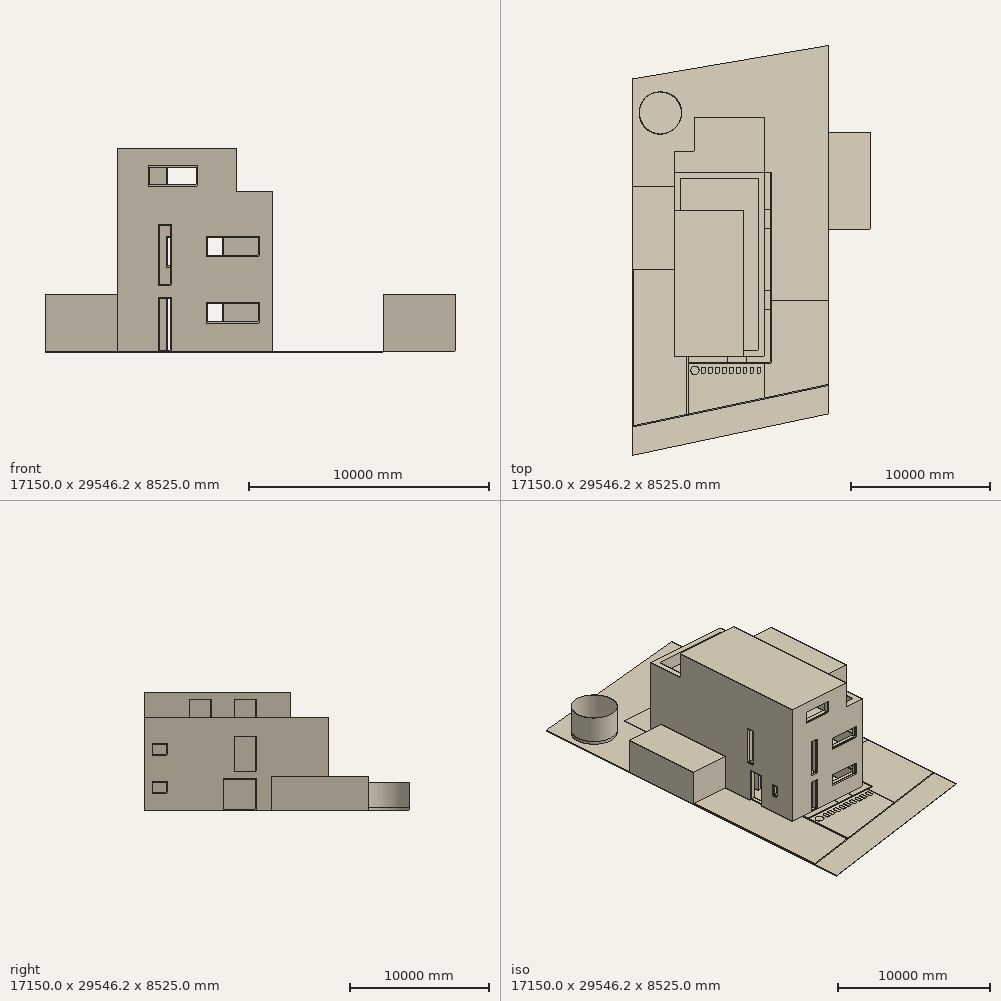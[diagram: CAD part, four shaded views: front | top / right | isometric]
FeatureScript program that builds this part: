
annotation { "Feature Type Name" : "Feature", "Feature Type Description" : "" }
export const myFeature = defineFeature(function(context is Context, id is Id, definition is map)
    precondition{}
    {
        {
            var Q0;
            Q0=qCreatedBy(makeId("Top.planeOp"),FACE);
            var sketch = newSketch(context, id + "F0", { "sketchPlane" : qUnion([Q0])});
            skLineSegment(sketch, "E0.bottom", {"start": v(0, 13250) * mm, "end": v(6500, 13250) * mm});
            skLineSegment(sketch, "E0.top", {"start": v(0, 0) * mm, "end": v(6500, 0) * mm});
            skLineSegment(sketch, "E0.left", {"start": v(0, 13250) * mm, "end": v(0, 0) * mm});
            skLineSegment(sketch, "E0.right", {"start": v(6500, 13250) * mm, "end": v(6500, 0) * mm});
            skSolve(sketch);
        }
        {
            var Q0;
            Q0=qCreatedBy(makeId("Top.planeOp"),FACE);
            var sketch = newSketch(context, id + "F1", { "sketchPlane" : qUnion([Q0])});
            skLineSegment(sketch, "E1", {"start": v(2050, 13250) * mm, "end": v(0, 13250) * mm});
            skLineSegment(sketch, "E2", {"start": v(0, 13250) * mm, "end": v(0, 4000) * mm});
            skLineSegment(sketch, "E3", {"start": v(0, 4000) * mm, "end": v(365, 4000) * mm});
            skLineSegment(sketch, "E4", {"start": v(365, 4000) * mm, "end": v(365, 12885) * mm});
            skLineSegment(sketch, "E5", {"start": v(365, 12885) * mm, "end": v(2050, 12885) * mm});
            skLineSegment(sketch, "E6", {"start": v(2050, 12885) * mm, "end": v(2050, 13250) * mm});
            skLineSegment(sketch, "E7", {"start": v(2050, 13067.5) * mm, "end": v(4450, 13067.5) * mm, "construction": true});
            skLineSegment(sketch, "E8", {"start": v(4450, 12885) * mm, "end": v(4450, 13250) * mm});
            skLineSegment(sketch, "E9", {"start": v(4450, 13250) * mm, "end": v(6500, 13250) * mm});
            skLineSegment(sketch, "E10", {"start": v(6500, 13250) * mm, "end": v(6500, 8065) * mm});
            skLineSegment(sketch, "E11", {"start": v(6500, 8065) * mm, "end": v(6135, 8065) * mm});
            skLineSegment(sketch, "E12", {"start": v(6135, 8065) * mm, "end": v(6135, 12885) * mm});
            skLineSegment(sketch, "E13", {"start": v(6135, 12885) * mm, "end": v(4450, 12885) * mm});
            skLineSegment(sketch, "E14", {"start": v(6317.5, 8065) * mm, "end": v(6317.5, 5665) * mm, "construction": true});
            skLineSegment(sketch, "E15.bottom", {"start": v(6135, 5665) * mm, "end": v(6500, 5665) * mm});
            skLineSegment(sketch, "E15.top", {"start": v(6135, 1655) * mm, "end": v(6500, 1655) * mm, "construction": true});
            skLineSegment(sketch, "E15.left", {"start": v(6135, 5665) * mm, "end": v(6135, 1655) * mm});
            skLineSegment(sketch, "E15.right", {"start": v(6500, 5665) * mm, "end": v(6500, 1655) * mm});
            skLineSegment(sketch, "E16", {"start": v(6135, 1655) * mm, "end": v(6135, 555) * mm});
            skLineSegment(sketch, "E17", {"start": v(6135, 555) * mm, "end": v(6500, 555) * mm, "construction": true});
            skLineSegment(sketch, "E18", {"start": v(6500, 555) * mm, "end": v(6500, 1655) * mm});
            skLineSegment(sketch, "E19", {"start": v(6135, 555) * mm, "end": v(6135, 365) * mm});
            skLineSegment(sketch, "E20", {"start": v(6135, 365) * mm, "end": v(5945, 365) * mm});
            skLineSegment(sketch, "E21", {"start": v(5945, 365) * mm, "end": v(5945, 0) * mm, "construction": true});
            skLineSegment(sketch, "E22", {"start": v(5945, 0) * mm, "end": v(6500, 0) * mm});
            skLineSegment(sketch, "E23", {"start": v(6500, 0) * mm, "end": v(6500, 555) * mm});
            skLineSegment(sketch, "E24", {"start": v(5945, 365) * mm, "end": v(3745, 365) * mm});
            skLineSegment(sketch, "E25", {"start": v(3745, 365) * mm, "end": v(3745, 0) * mm, "construction": true});
            skLineSegment(sketch, "E26", {"start": v(3745, 0) * mm, "end": v(5945, 0) * mm});
            skLineSegment(sketch, "E27", {"start": v(3745, 365) * mm, "end": v(2280, 365) * mm});
            skLineSegment(sketch, "E28", {"start": v(2280, 365) * mm, "end": v(2280, 0) * mm});
            skLineSegment(sketch, "E29", {"start": v(2280, 0) * mm, "end": v(3745, 0) * mm});
            skLineSegment(sketch, "E30", {"start": v(2280, 365) * mm, "end": v(1710, 365) * mm, "construction": true});
            skLineSegment(sketch, "E31", {"start": v(1710, 365) * mm, "end": v(1710, 0) * mm});
            skLineSegment(sketch, "E32", {"start": v(1710, 0) * mm, "end": v(2280, 0) * mm, "construction": true});
            skLineSegment(sketch, "E33", {"start": v(1710, 0) * mm, "end": v(0, 0) * mm});
            skLineSegment(sketch, "E34", {"start": v(0, 0) * mm, "end": v(0, 1400) * mm});
            skLineSegment(sketch, "E35", {"start": v(0, 1400) * mm, "end": v(365, 1400) * mm, "construction": true});
            skLineSegment(sketch, "E36", {"start": v(365, 1400) * mm, "end": v(365, 365) * mm});
            skLineSegment(sketch, "E37", {"start": v(365, 365) * mm, "end": v(1710, 365) * mm});
            skLineSegment(sketch, "E38", {"start": v(0, 1400) * mm, "end": v(0, 1900) * mm});
            skLineSegment(sketch, "E39", {"start": v(0, 1900) * mm, "end": v(365, 1900) * mm, "construction": true});
            skLineSegment(sketch, "E40", {"start": v(365, 1900) * mm, "end": v(365, 1400) * mm});
            skLineSegment(sketch, "E41", {"start": v(0, 1900) * mm, "end": v(0, 2900) * mm});
            skLineSegment(sketch, "E42", {"start": v(0, 2900) * mm, "end": v(365, 2900) * mm});
            skLineSegment(sketch, "E43", {"start": v(365, 2900) * mm, "end": v(365, 1900) * mm});
            skLineSegment(sketch, "E44", {"start": v(182.5, 2900) * mm, "end": v(182.5, 4000) * mm, "construction": true});
            skLineSegment(sketch, "E45.bottom", {"start": v(1305, 4500) * mm, "end": v(1455, 4500) * mm});
            skLineSegment(sketch, "E45.top", {"start": v(1305, 8000) * mm, "end": v(1455, 8000) * mm});
            skLineSegment(sketch, "E45.left", {"start": v(1305, 4500) * mm, "end": v(1305, 8000) * mm});
            skLineSegment(sketch, "E45.right", {"start": v(1455, 4500) * mm, "end": v(1455, 8000) * mm});
            skLineSegment(sketch, "E46", {"start": v(365, 2900) * mm, "end": v(1455, 2900) * mm});
            skLineSegment(sketch, "E47", {"start": v(1455, 2900) * mm, "end": v(1455, 365) * mm});
            skLineSegment(sketch, "E48", {"start": v(2955, 365) * mm, "end": v(2955, 2760) * mm});
            skLineSegment(sketch, "E49", {"start": v(2955, 2760) * mm, "end": v(2455, 2760) * mm});
            skLineSegment(sketch, "E50", {"start": v(2455, 2760) * mm, "end": v(2455, 2860) * mm});
            skLineSegment(sketch, "E51", {"start": v(2455, 2860) * mm, "end": v(3055, 2860) * mm});
            skLineSegment(sketch, "E52", {"start": v(3055, 2860) * mm, "end": v(3055, 365) * mm});
            skLineSegment(sketch, "E53.bottom", {"start": v(365, 2750) * mm, "end": v(1355, 2750) * mm});
            skLineSegment(sketch, "E53.right", {"start": v(1355, 2750) * mm, "end": v(1355, 365) * mm});
            skSolve(sketch);
        }
        {
            var Q0;
            Q0 = qSketchRegion(id + "F0", true);
            extrude(context, id + "F2", {"entities" : qUnion([Q0]), "oppositeDirection" : true, "depth" : 25 * mm, "offsetDistance" : 25 * mm});
        }
        {
            var Q0;
            Q0 = qSketchRegion(id + "F1", true);
            extrude(context, id + "F3", {"entities" : qUnion([Q0]), "depth" : 2270 * mm, "offsetDistance" : 25 * mm});
        }
        {
            var Q0;
            Q0=qCreatedBy(makeId("Top.planeOp"),FACE);
            cPlane(context, id + "F4", {"entities" : qUnion([Q0]), "cplaneType" : CPlaneType.OFFSET, "offset" : 1200 * mm, "width" : 150 * mm, "height" : 150 * mm});
        }
        {
            var Q0;
            Q0=qCreatedBy(id+"F4.planeOp",FACE);
            var sketch = newSketch(context, id + "F5", { "sketchPlane" : qUnion([Q0])});
            skLineSegment(sketch, "E54.bottom", {"start": v(6135, 1655) * mm, "end": v(6500, 1655) * mm});
            skLineSegment(sketch, "E54.top", {"start": v(6135, 555) * mm, "end": v(6500, 555) * mm});
            skLineSegment(sketch, "E54.left", {"start": v(6135, 1655) * mm, "end": v(6135, 555) * mm});
            skLineSegment(sketch, "E54.right", {"start": v(6500, 1655) * mm, "end": v(6500, 555) * mm});
            skLineSegment(sketch, "E55.bottom", {"start": v(5945, 365) * mm, "end": v(3745, 365) * mm});
            skLineSegment(sketch, "E55.top", {"start": v(5945, 0) * mm, "end": v(3745, 0) * mm});
            skLineSegment(sketch, "E55.left", {"start": v(5945, 365) * mm, "end": v(5945, 0) * mm});
            skLineSegment(sketch, "E55.right", {"start": v(3745, 365) * mm, "end": v(3745, 0) * mm});
            skLineSegment(sketch, "E56.bottom", {"start": v(365, 1400) * mm, "end": v(0, 1400) * mm});
            skLineSegment(sketch, "E56.top", {"start": v(365, 1900) * mm, "end": v(0, 1900) * mm});
            skLineSegment(sketch, "E56.left", {"start": v(0, 1900) * mm, "end": v(0, 1400) * mm});
            skLineSegment(sketch, "E56.right", {"start": v(365, 1900) * mm, "end": v(365, 1400) * mm});
            skSolve(sketch);
        }
        {
            var Q0;
            Q0 = qSketchRegion(id + "F5", true);
            extrude(context, id + "F6", {"entities" : qUnion([Q0]), "operationType" : NewBodyOperationType.REMOVE, "depth" : 850 * mm, "offsetDistance" : 25 * mm});
        }
        {
            var Q0;
            Q0=makeQuery(id+"F3.opExtrude","CAP_FACE",FACE,{"disambiguationData":[OSD([sQuery(id+"F1.wireOp",EDGE,"E31"),sQuery(id+"F1.wireOp",EDGE,"E33"),sQuery(id+"F1.wireOp",EDGE,"E34"),sQuery(id+"F1.wireOp",EDGE,"E36"),sQuery(id+"F1.wireOp",EDGE,"E37"),sQuery(id+"F1.wireOp",EDGE,"E38"),sQuery(id+"F1.wireOp",EDGE,"E40"),sQuery(id+"F1.wireOp",EDGE,"E41"),sQuery(id+"F1.wireOp",EDGE,"E42"),sQuery(id+"F1.wireOp",EDGE,"E43"),sQuery(id+"F1.wireOp",EDGE,"E46"),sQuery(id+"F1.wireOp",EDGE,"E47"),sQuery(id+"F1.wireOp",EDGE,"E53.bottom"),sQuery(id+"F1.wireOp",EDGE,"E53.right")])],"isStart":false});
            var sketch = newSketch(context, id + "F7", { "sketchPlane" : qUnion([Q0])});
            skLineSegment(sketch, "E57.bottom", {"start": v(0, 0) * mm, "end": v(6500, 0) * mm});
            skLineSegment(sketch, "E57.top", {"start": v(0, 13250) * mm, "end": v(6500, 13250) * mm});
            skLineSegment(sketch, "E57.left", {"start": v(0, 0) * mm, "end": v(0, 13250) * mm});
            skLineSegment(sketch, "E57.right", {"start": v(6500, 0) * mm, "end": v(6500, 13250) * mm});
            skLineSegment(sketch, "E58.bottom", {"start": v(365, 12885) * mm, "end": v(6135, 12885) * mm});
            skLineSegment(sketch, "E58.top", {"start": v(365, 365) * mm, "end": v(1355, 365) * mm});
            skLineSegment(sketch, "E58.left", {"start": v(365, 12885) * mm, "end": v(365, 2900) * mm});
            skLineSegment(sketch, "E58.right", {"start": v(6135, 12885) * mm, "end": v(6135, 365) * mm});
            skLineSegment(sketch, "E59", {"start": v(365, 2750) * mm, "end": v(1355, 2750) * mm});
            skLineSegment(sketch, "E60", {"start": v(1355, 2750) * mm, "end": v(1355, 365) * mm});
            skLineSegment(sketch, "E61", {"start": v(365, 2900) * mm, "end": v(1455, 2900) * mm});
            skLineSegment(sketch, "E62", {"start": v(1455, 2900) * mm, "end": v(1455, 365) * mm});
            skLineSegment(sketch, "E63", {"start": v(2955, 365) * mm, "end": v(2955, 2760) * mm});
            skLineSegment(sketch, "E64", {"start": v(2955, 2760) * mm, "end": v(2455, 2760) * mm});
            skLineSegment(sketch, "E65", {"start": v(2455, 2760) * mm, "end": v(2455, 2860) * mm});
            skLineSegment(sketch, "E66", {"start": v(2455, 2860) * mm, "end": v(3055, 2860) * mm});
            skLineSegment(sketch, "E67", {"start": v(3055, 2860) * mm, "end": v(3055, 365) * mm});
            skLineSegment(sketch, "E68.bottom", {"start": v(1305, 4500) * mm, "end": v(1455, 4500) * mm});
            skLineSegment(sketch, "E68.top", {"start": v(1305, 8000) * mm, "end": v(1455, 8000) * mm});
            skLineSegment(sketch, "E68.left", {"start": v(1305, 4500) * mm, "end": v(1305, 8000) * mm});
            skLineSegment(sketch, "E68.right", {"start": v(1455, 4500) * mm, "end": v(1455, 8000) * mm});
            skLineSegment(sketch, "E69.trimOffspring", {"start": v(3055, 365) * mm, "end": v(6135, 365) * mm});
            skLineSegment(sketch, "E70.trimOffspring", {"start": v(1455, 365) * mm, "end": v(2955, 365) * mm});
            skLineSegment(sketch, "E71.trimOffspring", {"start": v(365, 2750) * mm, "end": v(365, 365) * mm});
            skSolve(sketch);
        }
        {
            var Q0;
            Q0 = qSketchRegion(id + "F7", true);
            extrude(context, id + "F8", {"entities" : qUnion([Q0]), "operationType" : NewBodyOperationType.ADD, "depth" : 300 * mm, "offsetDistance" : 25 * mm});
        }
        {
            var Q0;
            Q0=makeQuery(id+"F3.opExtrude","CAP_FACE",FACE,{"disambiguationData":[OSD([sQuery(id+"F1.wireOp",EDGE,"E45.bottom"),sQuery(id+"F1.wireOp",EDGE,"E45.top"),sQuery(id+"F1.wireOp",EDGE,"E45.left"),sQuery(id+"F1.wireOp",EDGE,"E45.right")])],"isStart":false});
            var sketch = newSketch(context, id + "F9", { "sketchPlane" : qUnion([Q0])});
            skLineSegment(sketch, "E72.bottom", {"start": v(1305, 8000) * mm, "end": v(1455, 8000) * mm});
            skLineSegment(sketch, "E72.top", {"start": v(1305, 4500) * mm, "end": v(1455, 4500) * mm});
            skLineSegment(sketch, "E72.left", {"start": v(1305, 8000) * mm, "end": v(1305, 4500) * mm});
            skLineSegment(sketch, "E72.right", {"start": v(1455, 8000) * mm, "end": v(1455, 4500) * mm});
            skSolve(sketch);
        }
        {
            var Q0;
            Q0 = qSketchRegion(id + "F9", true);
            extrude(context, id + "F10", {"entities" : qUnion([Q0]), "operationType" : NewBodyOperationType.ADD, "depth" : 300 * mm, "offsetDistance" : 25 * mm});
        }
        {
            var Q0;
            Q0=makeQuery(id+"F8.opExtrude","CAP_FACE",FACE,{"disambiguationData":[OSD([sQuery(id+"F7.wireOp",EDGE,"E57.bottom"),sQuery(id+"F7.wireOp",EDGE,"E57.top"),sQuery(id+"F7.wireOp",EDGE,"E57.left"),sQuery(id+"F7.wireOp",EDGE,"E57.right"),sQuery(id+"F7.wireOp",EDGE,"E58.bottom"),sQuery(id+"F7.wireOp",EDGE,"E58.top"),sQuery(id+"F7.wireOp",EDGE,"E58.left"),sQuery(id+"F7.wireOp",EDGE,"E58.right"),sQuery(id+"F7.wireOp",EDGE,"E59"),sQuery(id+"F7.wireOp",EDGE,"E60"),sQuery(id+"F7.wireOp",EDGE,"E61"),sQuery(id+"F7.wireOp",EDGE,"E62"),sQuery(id+"F7.wireOp",EDGE,"E63"),sQuery(id+"F7.wireOp",EDGE,"E64"),sQuery(id+"F7.wireOp",EDGE,"E65"),sQuery(id+"F7.wireOp",EDGE,"E66"),sQuery(id+"F7.wireOp",EDGE,"E67"),sQuery(id+"F7.wireOp",EDGE,"E69.trimOffspring"),sQuery(id+"F7.wireOp",EDGE,"E70.trimOffspring"),sQuery(id+"F7.wireOp",EDGE,"E71.trimOffspring")])],"isStart":false});
            var sketch = newSketch(context, id + "F11", { "sketchPlane" : qUnion([Q0])});
            skLineSegment(sketch, "E73.bottom", {"start": v(0, 13250) * mm, "end": v(6500, 13250) * mm});
            skLineSegment(sketch, "E73.top", {"start": v(0, 0) * mm, "end": v(6500, 0) * mm});
            skLineSegment(sketch, "E73.left", {"start": v(0, 13250) * mm, "end": v(0, 0) * mm});
            skLineSegment(sketch, "E73.right", {"start": v(6500, 13250) * mm, "end": v(6500, 0) * mm});
            skSolve(sketch);
        }
        {
            var Q0;
            Q0 = qSketchRegion(id + "F11", true);
            extrude(context, id + "F12", {"entities" : qUnion([Q0]), "operationType" : NewBodyOperationType.ADD, "depth" : 200 * mm, "offsetDistance" : 25 * mm});
        }
        {
            var Q0;
            Q0=makeQuery(id+"F12.opExtrude","CAP_FACE",FACE,{"disambiguationData":[OSD([sQuery(id+"F11.wireOp",EDGE,"E73.bottom"),sQuery(id+"F11.wireOp",EDGE,"E73.top"),sQuery(id+"F11.wireOp",EDGE,"E73.left"),sQuery(id+"F11.wireOp",EDGE,"E73.right")])],"isStart":false});
            var sketch = newSketch(context, id + "F13", { "sketchPlane" : qUnion([Q0])});
            skLineSegment(sketch, "E74.bottom", {"start": v(0, 13250) * mm, "end": v(2050, 13250) * mm});
            skLineSegment(sketch, "E74.top", {"start": v(0, 0) * mm, "end": v(1710, 0) * mm});
            skLineSegment(sketch, "E74.left", {"start": v(0, 13250) * mm, "end": v(0, 4210) * mm});
            skLineSegment(sketch, "E74.right", {"start": v(6500, 13250) * mm, "end": v(6500, 8065) * mm});
            skLineSegment(sketch, "E75.bottom", {"start": v(365, 12885) * mm, "end": v(2050, 12885) * mm});
            skLineSegment(sketch, "E75.top", {"start": v(365, 365) * mm, "end": v(1710, 365) * mm});
            skLineSegment(sketch, "E75.left", {"start": v(365, 12885) * mm, "end": v(365, 4210) * mm});
            skLineSegment(sketch, "E75.right", {"start": v(6135, 12885) * mm, "end": v(6135, 8065) * mm});
            skLineSegment(sketch, "E76", {"start": v(2050, 13250) * mm, "end": v(2050, 12885) * mm, "construction": true});
            skLineSegment(sketch, "E77", {"start": v(2050, 13250) * mm, "end": v(4450, 13250) * mm});
            skLineSegment(sketch, "E78", {"start": v(4450, 12885) * mm, "end": v(6135, 12885) * mm});
            skLineSegment(sketch, "E79", {"start": v(2050, 12885) * mm, "end": v(4450, 12885) * mm});
            skLineSegment(sketch, "E80", {"start": v(4450, 13250) * mm, "end": v(4450, 12885) * mm, "construction": true});
            skLineSegment(sketch, "E81", {"start": v(4450, 13250) * mm, "end": v(6500, 13250) * mm});
            skLineSegment(sketch, "E82", {"start": v(6135, 8065) * mm, "end": v(6500, 8065) * mm});
            skLineSegment(sketch, "E83", {"start": v(6135, 6465) * mm, "end": v(6500, 6465) * mm});
            skLineSegment(sketch, "E84.trimOffspring", {"start": v(6135, 6465) * mm, "end": v(6135, 365) * mm});
            skLineSegment(sketch, "E85.trimOffspring", {"start": v(6500, 6465) * mm, "end": v(6500, 0) * mm});
            skLineSegment(sketch, "E86", {"start": v(6135, 1655) * mm, "end": v(6500, 1655) * mm, "construction": true});
            skLineSegment(sketch, "E87", {"start": v(6135, 555) * mm, "end": v(6500, 555) * mm, "construction": true});
            skLineSegment(sketch, "E88", {"start": v(5945, 365) * mm, "end": v(5945, 0) * mm, "construction": true});
            skLineSegment(sketch, "E89", {"start": v(3745, 365) * mm, "end": v(3745, 0) * mm, "construction": true});
            skLineSegment(sketch, "E90", {"start": v(1710, 365) * mm, "end": v(1710, 0) * mm});
            skLineSegment(sketch, "E91", {"start": v(2280, 365) * mm, "end": v(2280, 0) * mm});
            skLineSegment(sketch, "E92.trimOffspring", {"start": v(2280, 365) * mm, "end": v(6135, 365) * mm});
            skLineSegment(sketch, "E93.trimOffspring", {"start": v(2280, 0) * mm, "end": v(6500, 0) * mm});
            skLineSegment(sketch, "E94", {"start": v(0, 3640) * mm, "end": v(365, 3640) * mm});
            skLineSegment(sketch, "E95", {"start": v(0, 4210) * mm, "end": v(365, 4210) * mm});
            skLineSegment(sketch, "E96.trimOffspring", {"start": v(0, 3640) * mm, "end": v(0, 0) * mm});
            skLineSegment(sketch, "E97.trimOffspring", {"start": v(365, 3640) * mm, "end": v(365, 365) * mm});
            skSolve(sketch);
        }
        {
            var Q0;
            Q0 = qSketchRegion(id + "F13", true);
            extrude(context, id + "F14", {"entities" : qUnion([Q0]), "operationType" : NewBodyOperationType.ADD, "depth" : 2570 * mm, "offsetDistance" : 25 * mm});
        }
        {
            var Q0;
            Q0=makeQuery(id+"F12.opExtrude","CAP_FACE",FACE,{"disambiguationData":[OSD([sQuery(id+"F11.wireOp",EDGE,"E73.bottom"),sQuery(id+"F11.wireOp",EDGE,"E73.top"),sQuery(id+"F11.wireOp",EDGE,"E73.left"),sQuery(id+"F11.wireOp",EDGE,"E73.right")])],"isStart":false});
            cPlane(context, id + "F15", {"entities" : qUnion([Q0]), "cplaneType" : CPlaneType.OFFSET, "offset" : 1200 * mm, "width" : 150 * mm, "height" : 150 * mm});
        }
        {
            var Q0;
            Q0=qCreatedBy(id+"F15.planeOp",FACE);
            var sketch = newSketch(context, id + "F16", { "sketchPlane" : qUnion([Q0])});
            skLineSegment(sketch, "E98.bottom", {"start": v(3745, 365) * mm, "end": v(5945, 365) * mm});
            skLineSegment(sketch, "E98.top", {"start": v(3745, 0) * mm, "end": v(5945, 0) * mm});
            skLineSegment(sketch, "E98.left", {"start": v(3745, 365) * mm, "end": v(3745, 0) * mm});
            skLineSegment(sketch, "E98.right", {"start": v(5945, 365) * mm, "end": v(5945, 0) * mm});
            skLineSegment(sketch, "E99.bottom", {"start": v(6135, 1655) * mm, "end": v(6500, 1655) * mm});
            skLineSegment(sketch, "E99.top", {"start": v(6135, 555) * mm, "end": v(6500, 555) * mm});
            skLineSegment(sketch, "E99.left", {"start": v(6135, 1655) * mm, "end": v(6135, 555) * mm});
            skLineSegment(sketch, "E99.right", {"start": v(6500, 1655) * mm, "end": v(6500, 555) * mm});
            skSolve(sketch);
        }
        {
            var Q0;
            Q0 = qSketchRegion(id + "F16", true);
            extrude(context, id + "F17", {"entities" : qUnion([Q0]), "operationType" : NewBodyOperationType.REMOVE, "depth" : 850 * mm, "offsetDistance" : 25 * mm});
        }
        {
            var Q0;
            Q0=makeQuery(id+"F14.opExtrude","CAP_FACE",FACE,{"disambiguationData":[OSD([sQuery(id+"F13.wireOp",EDGE,"E74.bottom"),sQuery(id+"F13.wireOp",EDGE,"E74.left"),sQuery(id+"F13.wireOp",EDGE,"E74.right"),sQuery(id+"F13.wireOp",EDGE,"E75.bottom"),sQuery(id+"F13.wireOp",EDGE,"E75.left"),sQuery(id+"F13.wireOp",EDGE,"E75.right"),sQuery(id+"F13.wireOp",EDGE,"E77"),sQuery(id+"F13.wireOp",EDGE,"E78"),sQuery(id+"F13.wireOp",EDGE,"E79"),sQuery(id+"F13.wireOp",EDGE,"E81"),sQuery(id+"F13.wireOp",EDGE,"E82"),sQuery(id+"F13.wireOp",EDGE,"E95")])],"isStart":false});
            var sketch = newSketch(context, id + "F18", { "sketchPlane" : qUnion([Q0])});
            skLineSegment(sketch, "E100.bottom", {"start": v(0, 13250) * mm, "end": v(6500, 13250) * mm});
            skLineSegment(sketch, "E100.top", {"start": v(0, 0) * mm, "end": v(6500, 0) * mm});
            skLineSegment(sketch, "E100.left", {"start": v(0, 13250) * mm, "end": v(0, 0) * mm});
            skLineSegment(sketch, "E100.right", {"start": v(6500, 13250) * mm, "end": v(6500, 0) * mm});
            skLineSegment(sketch, "E101.bottom", {"start": v(365, 12885) * mm, "end": v(6135, 12885) * mm});
            skLineSegment(sketch, "E101.top", {"start": v(365, 365) * mm, "end": v(6135, 365) * mm});
            skLineSegment(sketch, "E101.left", {"start": v(365, 12885) * mm, "end": v(365, 365) * mm});
            skLineSegment(sketch, "E101.right", {"start": v(6135, 12885) * mm, "end": v(6135, 365) * mm});
            skSolve(sketch);
        }
        {
            var Q0;
            Q0 = qSketchRegion(id + "F18", true);
            extrude(context, id + "F19", {"entities" : qUnion([Q0]), "operationType" : NewBodyOperationType.ADD, "depth" : 300 * mm, "offsetDistance" : 25 * mm});
        }
        {
            var Q0;
            Q0=makeQuery(id+"F13.imprint","IMPRINT",FACE,{"disambiguationData":[TD([[makeQuery(id+"F13.imprint","IMPRINT",EDGE,{"derivedFrom":sQuery(id+"F13.wireOp",EDGE,"E75.bottom")}),-1.0]])]});
            cPlane(context, id + "F20", {"entities" : qUnion([Q0]), "cplaneType" : CPlaneType.OFFSET, "offset" : 770 * mm, "width" : 150 * mm, "height" : 150 * mm});
        }
        {
            var Q0;
            Q0=qCreatedBy(id+"F20.planeOp",FACE);
            var sketch = newSketch(context, id + "F21", { "sketchPlane" : qUnion([Q0])});
            skLineSegment(sketch, "E102.bottom", {"start": v(2050, 13250) * mm, "end": v(4450, 13250) * mm});
            skLineSegment(sketch, "E102.top", {"start": v(2050, 12885) * mm, "end": v(4450, 12885) * mm});
            skLineSegment(sketch, "E102.left", {"start": v(2050, 13250) * mm, "end": v(2050, 12885) * mm});
            skLineSegment(sketch, "E102.right", {"start": v(4450, 13250) * mm, "end": v(4450, 12885) * mm});
            skSolve(sketch);
        }
        {
            var Q0;
            Q0 = qSketchRegion(id + "F21", true);
            extrude(context, id + "F22", {"entities" : qUnion([Q0]), "operationType" : NewBodyOperationType.REMOVE, "depth" : 1280 * mm, "offsetDistance" : 25 * mm});
        }
        {
            var Q0;
            Q0=makeQuery(id+"F19.opExtrude","CAP_FACE",FACE,{"disambiguationData":[OSD([sQuery(id+"F18.wireOp",EDGE,"E100.bottom"),sQuery(id+"F18.wireOp",EDGE,"E100.top"),sQuery(id+"F18.wireOp",EDGE,"E100.left"),sQuery(id+"F18.wireOp",EDGE,"E100.right"),sQuery(id+"F18.wireOp",EDGE,"E101.bottom"),sQuery(id+"F18.wireOp",EDGE,"E101.top"),sQuery(id+"F18.wireOp",EDGE,"E101.left"),sQuery(id+"F18.wireOp",EDGE,"E101.right")])],"isStart":false});
            var sketch = newSketch(context, id + "F23", { "sketchPlane" : qUnion([Q0])});
            skLineSegment(sketch, "E103.bottom", {"start": v(0, 13250) * mm, "end": v(6500, 13250) * mm});
            skLineSegment(sketch, "E103.top", {"start": v(0, 0) * mm, "end": v(6500, 0) * mm});
            skLineSegment(sketch, "E103.left", {"start": v(0, 13250) * mm, "end": v(0, 0) * mm});
            skLineSegment(sketch, "E103.right", {"start": v(6500, 13250) * mm, "end": v(6500, 0) * mm});
            skSolve(sketch);
        }
        {
            var Q0;
            Q0 = qSketchRegion(id + "F23", true);
            extrude(context, id + "F24", {"entities" : qUnion([Q0]), "operationType" : NewBodyOperationType.ADD, "depth" : 200 * mm, "offsetDistance" : 25 * mm});
        }
        {
            var Q0;
            Q0=makeQuery(id+"F24.opExtrude","CAP_FACE",FACE,{"disambiguationData":[OSD([sQuery(id+"F23.wireOp",EDGE,"E103.bottom"),sQuery(id+"F23.wireOp",EDGE,"E103.top"),sQuery(id+"F23.wireOp",EDGE,"E103.left"),sQuery(id+"F23.wireOp",EDGE,"E103.right")])],"isStart":false});
            var sketch = newSketch(context, id + "F25", { "sketchPlane" : qUnion([Q0])});
            skLineSegment(sketch, "E104.bottom", {"start": v(0, 0) * mm, "end": v(1310, 0) * mm});
            skLineSegment(sketch, "E104.top", {"start": v(0, 10500) * mm, "end": v(2045, 10500) * mm});
            skLineSegment(sketch, "E104.left", {"start": v(0, 0) * mm, "end": v(0, 10500) * mm});
            skLineSegment(sketch, "E104.right", {"start": v(5000, 0) * mm, "end": v(5000, 3235) * mm});
            skLineSegment(sketch, "E105.bottom", {"start": v(365, 10135) * mm, "end": v(2045, 10135) * mm});
            skLineSegment(sketch, "E105.top", {"start": v(365, 365) * mm, "end": v(1310, 365) * mm});
            skLineSegment(sketch, "E105.left", {"start": v(365, 10135) * mm, "end": v(365, 365) * mm});
            skLineSegment(sketch, "E105.right", {"start": v(4635, 10135) * mm, "end": v(4635, 8065) * mm});
            skLineSegment(sketch, "E106", {"start": v(2045, 10135) * mm, "end": v(2045, 10500) * mm});
            skLineSegment(sketch, "E107", {"start": v(4445, 10500) * mm, "end": v(4445, 10135) * mm});
            skLineSegment(sketch, "E108.trimOffspring", {"start": v(4445, 10500) * mm, "end": v(5000, 10500) * mm});
            skLineSegment(sketch, "E109.trimOffspring", {"start": v(4445, 10135) * mm, "end": v(4635, 10135) * mm});
            skLineSegment(sketch, "E110", {"start": v(4635, 8065) * mm, "end": v(5000, 8065) * mm});
            skLineSegment(sketch, "E111", {"start": v(4635, 6465) * mm, "end": v(5000, 6465) * mm});
            skLineSegment(sketch, "E112.trimOffspring", {"start": v(4635, 6465) * mm, "end": v(4635, 4835) * mm});
            skLineSegment(sketch, "E113.trimOffspring", {"start": v(5000, 8065) * mm, "end": v(5000, 10500) * mm});
            skLineSegment(sketch, "E114", {"start": v(4635, 4835) * mm, "end": v(5000, 4835) * mm});
            skLineSegment(sketch, "E115", {"start": v(4635, 3235) * mm, "end": v(5000, 3235) * mm});
            skLineSegment(sketch, "E116.trimOffspring", {"start": v(4635, 3235) * mm, "end": v(4635, 365) * mm});
            skLineSegment(sketch, "E117.trimOffspring", {"start": v(5000, 4835) * mm, "end": v(5000, 6465) * mm});
            skLineSegment(sketch, "E118", {"start": v(3360, 365) * mm, "end": v(3360, 0) * mm, "construction": true});
            skLineSegment(sketch, "E119", {"start": v(1310, 365) * mm, "end": v(1310, 0) * mm, "construction": true});
            skLineSegment(sketch, "E120.trimOffspring", {"start": v(3360, 365) * mm, "end": v(4635, 365) * mm});
            skLineSegment(sketch, "E121.trimOffspring", {"start": v(3360, 0) * mm, "end": v(5000, 0) * mm});
            skLineSegment(sketch, "E122", {"start": v(365, 365) * mm, "end": v(0, 365) * mm, "construction": true});
            skLineSegment(sketch, "E123", {"start": v(1310, 365) * mm, "end": v(3360, 365) * mm});
            skLineSegment(sketch, "E124", {"start": v(1310, 0) * mm, "end": v(3360, 0) * mm});
            skSolve(sketch);
        }
        {
            var Q0;
            Q0 = qSketchRegion(id + "F25", true);
            extrude(context, id + "F26", {"entities" : qUnion([Q0]), "operationType" : NewBodyOperationType.ADD, "depth" : 2160 * mm, "offsetDistance" : 25 * mm});
        }
        {
            var Q0;
            Q0=makeQuery(id+"F24.opExtrude","CAP_FACE",FACE,{"disambiguationData":[OSD([sQuery(id+"F23.wireOp",EDGE,"E103.bottom"),sQuery(id+"F23.wireOp",EDGE,"E103.top"),sQuery(id+"F23.wireOp",EDGE,"E103.left"),sQuery(id+"F23.wireOp",EDGE,"E103.right")])],"isStart":false});
            cPlane(context, id + "F27", {"entities" : qUnion([Q0]), "cplaneType" : CPlaneType.OFFSET, "offset" : 1090 * mm, "width" : 150 * mm, "height" : 150 * mm});
        }
        {
            var Q0;
            Q0=qCreatedBy(id+"F27.planeOp",FACE);
            var sketch = newSketch(context, id + "F28", { "sketchPlane" : qUnion([Q0])});
            skLineSegment(sketch, "E125.bottom", {"start": v(1310, 365) * mm, "end": v(3360, 365) * mm});
            skLineSegment(sketch, "E125.top", {"start": v(1310, 0) * mm, "end": v(3360, 0) * mm});
            skLineSegment(sketch, "E125.left", {"start": v(1310, 365) * mm, "end": v(1310, 0) * mm});
            skLineSegment(sketch, "E125.right", {"start": v(3360, 365) * mm, "end": v(3360, 0) * mm});
            skSolve(sketch);
        }
        {
            var Q0;
            Q0 = qSketchRegion(id + "F28", true);
            extrude(context, id + "F29", {"entities" : qUnion([Q0]), "operationType" : NewBodyOperationType.REMOVE, "depth" : 850 * mm, "offsetDistance" : 25 * mm});
        }
        {
            var Q0;
            Q0=makeQuery(id+"F26.opExtrude","CAP_FACE",FACE,{"disambiguationData":[OSD([sQuery(id+"F25.wireOp",EDGE,"E104.bottom"),sQuery(id+"F25.wireOp",EDGE,"E104.top"),sQuery(id+"F25.wireOp",EDGE,"E104.left"),sQuery(id+"F25.wireOp",EDGE,"E104.right"),sQuery(id+"F25.wireOp",EDGE,"E105.bottom"),sQuery(id+"F25.wireOp",EDGE,"E105.top"),sQuery(id+"F25.wireOp",EDGE,"E105.left"),sQuery(id+"F25.wireOp",EDGE,"E106"),sQuery(id+"F25.wireOp",EDGE,"E115"),sQuery(id+"F25.wireOp",EDGE,"E116.trimOffspring"),sQuery(id+"F25.wireOp",EDGE,"E120.trimOffspring"),sQuery(id+"F25.wireOp",EDGE,"E121.trimOffspring"),sQuery(id+"F25.wireOp",EDGE,"E123"),sQuery(id+"F25.wireOp",EDGE,"E124")])],"isStart":false});
            var sketch = newSketch(context, id + "F30", { "sketchPlane" : qUnion([Q0])});
            skLineSegment(sketch, "E126.bottom", {"start": v(0, 10500) * mm, "end": v(5000, 10500) * mm});
            skLineSegment(sketch, "E126.top", {"start": v(0, 0) * mm, "end": v(5000, 0) * mm});
            skLineSegment(sketch, "E126.left", {"start": v(0, 10500) * mm, "end": v(0, 0) * mm});
            skLineSegment(sketch, "E126.right", {"start": v(5000, 10500) * mm, "end": v(5000, 0) * mm});
            skLineSegment(sketch, "E127.bottom", {"start": v(4635, 365) * mm, "end": v(365, 365) * mm});
            skLineSegment(sketch, "E127.top", {"start": v(4635, 10135) * mm, "end": v(365, 10135) * mm});
            skLineSegment(sketch, "E127.left", {"start": v(4635, 365) * mm, "end": v(4635, 10135) * mm});
            skLineSegment(sketch, "E127.right", {"start": v(365, 365) * mm, "end": v(365, 10135) * mm});
            skSolve(sketch);
        }
        {
            var Q0;
            Q0 = qSketchRegion(id + "F30", true);
            extrude(context, id + "F31", {"entities" : qUnion([Q0]), "operationType" : NewBodyOperationType.ADD, "depth" : 300 * mm, "offsetDistance" : 25 * mm});
        }
        {
            var Q0;
            Q0=makeQuery(id+"F31.opExtrude","CAP_FACE",FACE,{"disambiguationData":[OSD([sQuery(id+"F30.wireOp",EDGE,"E126.bottom"),sQuery(id+"F30.wireOp",EDGE,"E126.top"),sQuery(id+"F30.wireOp",EDGE,"E126.left"),sQuery(id+"F30.wireOp",EDGE,"E126.right"),sQuery(id+"F30.wireOp",EDGE,"E127.bottom"),sQuery(id+"F30.wireOp",EDGE,"E127.top"),sQuery(id+"F30.wireOp",EDGE,"E127.left"),sQuery(id+"F30.wireOp",EDGE,"E127.right")])],"isStart":false});
            var sketch = newSketch(context, id + "F32", { "sketchPlane" : qUnion([Q0])});
            skLineSegment(sketch, "E128.bottom", {"start": v(0, 10500) * mm, "end": v(5000, 10500) * mm});
            skLineSegment(sketch, "E128.top", {"start": v(0, 0) * mm, "end": v(5000, 0) * mm});
            skLineSegment(sketch, "E128.left", {"start": v(0, 10500) * mm, "end": v(0, 0) * mm});
            skLineSegment(sketch, "E128.right", {"start": v(5000, 10500) * mm, "end": v(5000, 0) * mm});
            skSolve(sketch);
        }
        {
            var Q0;
            Q0 = qSketchRegion(id + "F32", true);
            extrude(context, id + "F33", {"entities" : qUnion([Q0]), "operationType" : NewBodyOperationType.ADD, "depth" : 200 * mm, "offsetDistance" : 25 * mm});
        }
        {
            var Q0;
            Q0=makeQuery(id+"F24.opExtrude","CAP_FACE",FACE,{"disambiguationData":[OSD([sQuery(id+"F23.wireOp",EDGE,"E103.bottom"),sQuery(id+"F23.wireOp",EDGE,"E103.top"),sQuery(id+"F23.wireOp",EDGE,"E103.left"),sQuery(id+"F23.wireOp",EDGE,"E103.right")])],"isStart":false});
            var sketch = newSketch(context, id + "F34", { "sketchPlane" : qUnion([Q0])});
            skLineSegment(sketch, "E129", {"start": v(440, 10500) * mm, "end": v(0, 10500) * mm});
            skLineSegment(sketch, "E130", {"start": v(0, 10500) * mm, "end": v(0, 13250) * mm});
            skLineSegment(sketch, "E131", {"start": v(0, 13250) * mm, "end": v(6500, 13250) * mm});
            skLineSegment(sketch, "E132", {"start": v(6500, 13250) * mm, "end": v(6500, 0) * mm});
            skLineSegment(sketch, "E133", {"start": v(6500, 0) * mm, "end": v(5000, 0) * mm});
            skLineSegment(sketch, "E134", {"start": v(5000, 0) * mm, "end": v(5000, 440) * mm});
            skLineSegment(sketch, "E135", {"start": v(5000, 440) * mm, "end": v(6060, 440) * mm});
            skLineSegment(sketch, "E136", {"start": v(6060, 440) * mm, "end": v(6060, 12810) * mm});
            skLineSegment(sketch, "E137", {"start": v(6060, 12810) * mm, "end": v(440, 12810) * mm});
            skLineSegment(sketch, "E138", {"start": v(440, 12810) * mm, "end": v(440, 10500) * mm});
            skLineSegment(sketch, "E139", {"start": v(6060, 12810) * mm, "end": v(6060, 13250) * mm, "construction": true});
            skLineSegment(sketch, "E140", {"start": v(6060, 12810) * mm, "end": v(6500, 12810) * mm, "construction": true});
            skSolve(sketch);
        }
        {
            var Q0;
            Q0 = qSketchRegion(id + "F34", true);
            extrude(context, id + "F35", {"entities" : qUnion([Q0]), "operationType" : NewBodyOperationType.ADD, "depth" : 850 * mm, "offsetDistance" : 25 * mm});
        }
        {
            var Q0;
            Q0=qCreatedBy(makeId("Top.planeOp"),FACE);
            var sketch = newSketch(context, id + "F36", { "sketchPlane" : qUnion([Q0])});
            skLineSegment(sketch, "E141", {"start": v(-3000, -5000) * mm, "end": v(11150, -2000) * mm});
            skLineSegment(sketch, "E142", {"start": v(11150, -2000) * mm, "end": v(11150, 22420) * mm});
            skLineSegment(sketch, "E143", {"start": v(11150, 22420) * mm, "end": v(-3000, 20000) * mm});
            skLineSegment(sketch, "E144", {"start": v(-3000, 20000) * mm, "end": v(-3000, -5000) * mm});
            skSolve(sketch);
        }
        {
            var Q0;
            Q0=qCreatedBy(makeId("Top.planeOp"),FACE);
            var sketch = newSketch(context, id + "F37", { "sketchPlane" : qUnion([Q0])});
            skLineSegment(sketch, "E145.bottom", {"start": v(-2850, 6250) * mm, "end": v(-3000, 6250) * mm});
            skLineSegment(sketch, "E145.top", {"start": v(-2600, 12250) * mm, "end": v(-3000, 12250) * mm});
            skLineSegment(sketch, "E145.left", {"start": v(-3000, 6250) * mm, "end": v(-3000, 12250) * mm});
            skLineSegment(sketch, "E145.right", {"start": v(0, 6250) * mm, "end": v(0, 12250) * mm});
            skLineSegment(sketch, "E146.bottom", {"start": v(-2850, 12100) * mm, "end": v(-2600, 12100) * mm});
            skLineSegment(sketch, "E146.left", {"start": v(-2850, 12100) * mm, "end": v(-2850, 6250) * mm});
            skLineSegment(sketch, "E146.right", {"start": v(-150, 12100) * mm, "end": v(-150, 6250) * mm});
            skLineSegment(sketch, "E147", {"start": v(-2600, 12250) * mm, "end": v(-2600, 12100) * mm});
            skLineSegment(sketch, "E148", {"start": v(-1750, 12250) * mm, "end": v(-1750, 12100) * mm});
            skLineSegment(sketch, "E149.trimOffspring", {"start": v(0, 12250) * mm, "end": v(-1750, 12250) * mm});
            skLineSegment(sketch, "E150.trimOffspring", {"start": v(-1750, 12100) * mm, "end": v(-150, 12100) * mm});
            skLineSegment(sketch, "E151", {"start": v(-2850, 12100) * mm, "end": v(-3000, 12100) * mm, "construction": true});
            skLineSegment(sketch, "E152", {"start": v(-150, 12100) * mm, "end": v(0, 12100) * mm, "construction": true});
            skLineSegment(sketch, "E153", {"start": v(-2600, 12175) * mm, "end": v(-1750, 12175) * mm, "construction": true});
            skLineSegment(sketch, "E154.trimOffspring", {"start": v(0, 6250) * mm, "end": v(-150, 6250) * mm});
            skSolve(sketch);
        }
        {
            var Q0;
            Q0 = qSketchRegion(id + "F37", true);
            extrude(context, id + "F38", {"entities" : qUnion([Q0]), "operationType" : NewBodyOperationType.ADD, "depth" : 2200 * mm, "offsetDistance" : 25 * mm});
        }
        {
            var Q0;
            Q0=qCreatedBy(makeId("Top.planeOp"),FACE);
            var sketch = newSketch(context, id + "F39", { "sketchPlane" : qUnion([Q0])});
            skLineSegment(sketch, "E155.bottom", {"start": v(-3000, 12250) * mm, "end": v(0, 12250) * mm});
            skLineSegment(sketch, "E155.top", {"start": v(-3000, 6250) * mm, "end": v(0, 6250) * mm});
            skLineSegment(sketch, "E155.left", {"start": v(-3000, 12250) * mm, "end": v(-3000, 6250) * mm});
            skLineSegment(sketch, "E155.right", {"start": v(0, 12250) * mm, "end": v(0, 6250) * mm});
            skSolve(sketch);
        }
        {
            var Q0;
            Q0 = qSketchRegion(id + "F39", true);
            extrude(context, id + "F40", {"entities" : qUnion([Q0]), "operationType" : NewBodyOperationType.ADD, "oppositeDirection" : true, "depth" : 25 * mm, "offsetDistance" : 25 * mm});
        }
        {
            var Q0;
            Q0=makeQuery(id+"F38.opExtrude","CAP_FACE",FACE,{"disambiguationData":[OSD([sQuery(id+"F37.wireOp",EDGE,"E145.right"),sQuery(id+"F37.wireOp",EDGE,"E146.right"),sQuery(id+"F37.wireOp",EDGE,"E148"),sQuery(id+"F37.wireOp",EDGE,"E149.trimOffspring"),sQuery(id+"F37.wireOp",EDGE,"E150.trimOffspring"),sQuery(id+"F37.wireOp",EDGE,"E154.trimOffspring")])],"isStart":false});
            var sketch = newSketch(context, id + "F41", { "sketchPlane" : qUnion([Q0])});
            skLineSegment(sketch, "E156.bottom", {"start": v(-3000, 12250) * mm, "end": v(0, 12250) * mm});
            skLineSegment(sketch, "E156.top", {"start": v(-3000, 6250) * mm, "end": v(0, 6250) * mm});
            skLineSegment(sketch, "E156.left", {"start": v(-3000, 12250) * mm, "end": v(-3000, 6250) * mm});
            skLineSegment(sketch, "E156.right", {"start": v(0, 12250) * mm, "end": v(0, 6250) * mm});
            skSolve(sketch);
        }
        {
            var Q0;
            Q0 = qSketchRegion(id + "F41", true);
            extrude(context, id + "F42", {"entities" : qUnion([Q0]), "operationType" : NewBodyOperationType.ADD, "depth" : 200 * mm, "offsetDistance" : 25 * mm});
        }
        {
            var Q0;
            Q0=qCreatedBy(makeId("Top.planeOp"),FACE);
            var sketch = newSketch(context, id + "F43", { "sketchPlane" : qUnion([Q0])});
            skLineSegment(sketch, "E157", {"start": v(-3000, 6250) * mm, "end": v(-2920, 6250) * mm});
            skLineSegment(sketch, "E158", {"start": v(920, 0) * mm, "end": v(1000, 0) * mm});
            skLineSegment(sketch, "E159", {"start": v(1000, 0) * mm, "end": v(1000, -4151.94) * mm});
            skLineSegment(sketch, "E160", {"start": v(1000, -4151.94) * mm, "end": v(920, -4168.9) * mm});
            skLineSegment(sketch, "E161", {"start": v(-2920, -4983.04) * mm, "end": v(-2920, 6250) * mm});
            skLineSegment(sketch, "E162", {"start": v(920, 0) * mm, "end": v(920, -4168.9) * mm});
            skLineSegment(sketch, "E163", {"start": v(-3000, -5000) * mm, "end": v(-3000, 6250) * mm});
            skLineSegment(sketch, "E164.trimOffspring", {"start": v(-2920, -4983.04) * mm, "end": v(-3000, -5000) * mm});
            skSolve(sketch);
        }
        {
            var Q0;
            Q0=qSketchRegion(id+"F43",true);
            extrude(context, id + "F44", {"entities" : qUnion([Q0]), "oppositeDirection" : true, "depth" : 25 * mm, "offsetDistance" : 25 * mm});
        }
        {
            var Q0;
            Q0=qCreatedBy(makeId("Top.planeOp"),FACE);
            var sketch = newSketch(context, id + "F45", { "sketchPlane" : qUnion([Q0])});
            skLineSegment(sketch, "E165", {"start": v(-2920, -4983.04) * mm, "end": v(920, -4168.9) * mm});
            skLineSegment(sketch, "E166", {"start": v(920, -4168.9) * mm, "end": v(920, 0) * mm});
            skLineSegment(sketch, "E167", {"start": v(920, 0) * mm, "end": v(0, 0) * mm});
            skLineSegment(sketch, "E168", {"start": v(0, 0) * mm, "end": v(0, 6250) * mm});
            skLineSegment(sketch, "E169", {"start": v(0, 6250) * mm, "end": v(-2920, 6250) * mm});
            skLineSegment(sketch, "E170", {"start": v(-2920, 6250) * mm, "end": v(-2920, -4983.04) * mm});
            skSolve(sketch);
        }
        {
            var Q0;
            Q0 = qSketchRegion(id + "F45", true);
            extrude(context, id + "F46", {"entities" : qUnion([Q0]), "oppositeDirection" : true, "depth" : 25 * mm, "offsetDistance" : 25 * mm});
        }
        {
            var Q0;
            Q0=qCreatedBy(makeId("Top.planeOp"),FACE);
            var sketch = newSketch(context, id + "F47", { "sketchPlane" : qUnion([Q0])});
            skLineSegment(sketch, "E171", {"start": v(1000, 0) * mm, "end": v(1000, -420) * mm});
            skLineSegment(sketch, "E172", {"start": v(1000, -420) * mm, "end": v(3880, -420) * mm});
            skLineSegment(sketch, "E173", {"start": v(6920, -420) * mm, "end": v(6920, 3400) * mm});
            skLineSegment(sketch, "E174", {"start": v(6920, 13250) * mm, "end": v(6500, 13250) * mm});
            skLineSegment(sketch, "E175", {"start": v(6500, 13250) * mm, "end": v(6500, 10580) * mm});
            skLineSegment(sketch, "E176", {"start": v(6500, 0) * mm, "end": v(5230, 0) * mm});
            skLineSegment(sketch, "E177", {"start": v(5230, 0) * mm, "end": v(5230, -420) * mm});
            skLineSegment(sketch, "E178", {"start": v(3880, 0) * mm, "end": v(3880, -420) * mm});
            skLineSegment(sketch, "E179", {"start": v(6500, 10580) * mm, "end": v(6920, 10580) * mm});
            skLineSegment(sketch, "E180", {"start": v(6500, 9230) * mm, "end": v(6920, 9230) * mm});
            skLineSegment(sketch, "E181", {"start": v(6500, 3400) * mm, "end": v(6920, 3400) * mm});
            skLineSegment(sketch, "E182", {"start": v(6500, 4750) * mm, "end": v(6920, 4750) * mm});
            skLineSegment(sketch, "E183.trimOffspring", {"start": v(3880, 0) * mm, "end": v(1000, 0) * mm});
            skLineSegment(sketch, "E184.trimOffspring", {"start": v(5230, -420) * mm, "end": v(6920, -420) * mm});
            skLineSegment(sketch, "E185.trimOffspring", {"start": v(6500, 3400) * mm, "end": v(6500, 0) * mm});
            skLineSegment(sketch, "E186.trimOffspring", {"start": v(6920, 4750) * mm, "end": v(6920, 9230) * mm});
            skLineSegment(sketch, "E187.trimOffspring", {"start": v(6500, 9230) * mm, "end": v(6500, 4750) * mm});
            skLineSegment(sketch, "E188.trimOffspring", {"start": v(6920, 10580) * mm, "end": v(6920, 13250) * mm});
            skSolve(sketch);
        }
        {
            var Q0;
            Q0 = qSketchRegion(id + "F47", true);
            extrude(context, id + "F48", {"entities" : qUnion([Q0]), "oppositeDirection" : true, "depth" : 25 * mm, "offsetDistance" : 25 * mm});
        }
        {
            var Q0;
            Q0=qCreatedBy(makeId("Top.planeOp"),FACE);
            var sketch = newSketch(context, id + "F49", { "sketchPlane" : qUnion([Q0])});
            skLineSegment(sketch, "E189", {"start": v(1000, -500) * mm, "end": v(1000, -420) * mm});
            skLineSegment(sketch, "E190", {"start": v(1000, -420) * mm, "end": v(6920, -420) * mm});
            skLineSegment(sketch, "E191", {"start": v(6920, -420) * mm, "end": v(6920, 13250) * mm});
            skLineSegment(sketch, "E192", {"start": v(6920, 13250) * mm, "end": v(7000, 13250) * mm});
            skLineSegment(sketch, "E193", {"start": v(7000, 13250) * mm, "end": v(7000, -500) * mm});
            skLineSegment(sketch, "E194", {"start": v(7000, -500) * mm, "end": v(1000, -500) * mm});
            skSolve(sketch);
        }
        {
            var Q0;
            Q0 = qSketchRegion(id + "F49", true);
            extrude(context, id + "F50", {"entities" : qUnion([Q0]), "oppositeDirection" : true, "depth" : 25 * mm, "offsetDistance" : 25 * mm});
        }
        {
            var Q0;
            Q0=qCreatedBy(makeId("Top.planeOp"),FACE);
            var sketch = newSketch(context, id + "F51", { "sketchPlane" : qUnion([Q0])});
            skLineSegment(sketch, "E195.bottom", {"start": v(3880, 0) * mm, "end": v(5230, 0) * mm});
            skLineSegment(sketch, "E195.top", {"start": v(3880, -420) * mm, "end": v(5230, -420) * mm});
            skLineSegment(sketch, "E195.left", {"start": v(3880, 0) * mm, "end": v(3880, -420) * mm});
            skLineSegment(sketch, "E195.right", {"start": v(5230, 0) * mm, "end": v(5230, -420) * mm});
            skLineSegment(sketch, "E196.bottom", {"start": v(6500, 4750) * mm, "end": v(6920, 4750) * mm});
            skLineSegment(sketch, "E196.top", {"start": v(6500, 3400) * mm, "end": v(6920, 3400) * mm});
            skLineSegment(sketch, "E196.left", {"start": v(6500, 4750) * mm, "end": v(6500, 3400) * mm});
            skLineSegment(sketch, "E196.right", {"start": v(6920, 4750) * mm, "end": v(6920, 3400) * mm});
            skLineSegment(sketch, "E197.bottom", {"start": v(6500, 10580) * mm, "end": v(6920, 10580) * mm});
            skLineSegment(sketch, "E197.top", {"start": v(6500, 9230) * mm, "end": v(6920, 9230) * mm});
            skLineSegment(sketch, "E197.left", {"start": v(6500, 10580) * mm, "end": v(6500, 9230) * mm});
            skLineSegment(sketch, "E197.right", {"start": v(6920, 10580) * mm, "end": v(6920, 9230) * mm});
            skSolve(sketch);
        }
        {
            var Q0;
            Q0=qSketchRegion(id+"F51",true);
            extrude(context, id + "F52", {"entities" : qUnion([Q0]), "oppositeDirection" : true, "depth" : 25 * mm, "offsetDistance" : 25 * mm});
        }
        {
            var Q0;
            Q0=qCreatedBy(makeId("Top.planeOp"),FACE);
            var sketch = newSketch(context, id + "F53", { "sketchPlane" : qUnion([Q0])});
            skLineSegment(sketch, "E198", {"start": v(1000, -4151.94) * mm, "end": v(1000, -500) * mm});
            skLineSegment(sketch, "E199", {"start": v(1000, -500) * mm, "end": v(6500, -500) * mm});
            skLineSegment(sketch, "E200", {"start": v(6500, -500) * mm, "end": v(6500, -2985.87) * mm});
            skLineSegment(sketch, "E201", {"start": v(6500, -2985.87) * mm, "end": v(1000, -4151.94) * mm});
            skSolve(sketch);
        }
        {
            var Q0;
            Q0 = qSketchRegion(id + "F53", true);
            extrude(context, id + "F54", {"entities" : qUnion([Q0]), "oppositeDirection" : true, "depth" : 25 * mm, "offsetDistance" : 25 * mm});
        }
        {
            var Q0;
            Q0=qCreatedBy(makeId("Top.planeOp"),FACE);
            var sketch = newSketch(context, id + "F55", { "sketchPlane" : qUnion([Q0])});
            skLineSegment(sketch, "E202", {"start": v(6500, -2985.87) * mm, "end": v(6500, -500) * mm});
            skLineSegment(sketch, "E203", {"start": v(6500, -500) * mm, "end": v(7000, -500) * mm});
            skLineSegment(sketch, "E204", {"start": v(7000, -500) * mm, "end": v(7000, 4075) * mm});
            skLineSegment(sketch, "E205", {"start": v(7000, 4075) * mm, "end": v(11150, 4075) * mm});
            skLineSegment(sketch, "E206", {"start": v(11150, 4075) * mm, "end": v(11150, -2000) * mm});
            skLineSegment(sketch, "E207", {"start": v(11150, -2000) * mm, "end": v(6500, -2985.87) * mm});
            skLineSegment(sketch, "E208", {"start": v(7000, 4075) * mm, "end": v(6920, 4075) * mm, "construction": true});
            skSolve(sketch);
        }
        {
            var Q0;
            Q0 = qSketchRegion(id + "F55", true);
            extrude(context, id + "F56", {"entities" : qUnion([Q0]), "oppositeDirection" : true, "depth" : 25 * mm, "offsetDistance" : 25 * mm});
        }
        {
            var Q0;
            Q0=qCreatedBy(makeId("Top.planeOp"),FACE);
            var sketch = newSketch(context, id + "F57", { "sketchPlane" : qUnion([Q0])});
            skLineSegment(sketch, "E209", {"start": v(0, 13250) * mm, "end": v(6500, 13250) * mm});
            skLineSegment(sketch, "E210", {"start": v(6500, 13250) * mm, "end": v(6500, 17250) * mm});
            skLineSegment(sketch, "E211", {"start": v(6500, 17250) * mm, "end": v(1500, 17250) * mm});
            skLineSegment(sketch, "E212", {"start": v(1500, 17250) * mm, "end": v(1500, 14750) * mm});
            skLineSegment(sketch, "E213", {"start": v(1500, 14750) * mm, "end": v(0, 14750) * mm});
            skLineSegment(sketch, "E214", {"start": v(0, 14750) * mm, "end": v(0, 13250) * mm});
            skSolve(sketch);
        }
        {
            var Q0;
            Q0 = qSketchRegion(id + "F57", true);
            extrude(context, id + "F58", {"entities" : qUnion([Q0]), "oppositeDirection" : true, "depth" : 25 * mm, "offsetDistance" : 25 * mm});
        }
        {
            var Q0;
            Q0=qCreatedBy(makeId("Top.planeOp"),FACE);
            var sketch = newSketch(context, id + "F59", { "sketchPlane" : qUnion([Q0])});
            skLineSegment(sketch, "E215.bottom", {"start": v(-3000, 20000) * mm, "end": v(11150, 22420) * mm});
            skLineSegment(sketch, "E215.top", {"start": v(7000, 4075) * mm, "end": v(11150, 4075) * mm});
            skLineSegment(sketch, "E215.right", {"start": v(11150, 4075) * mm, "end": v(11150, 22420) * mm});
            skLineSegment(sketch, "E216", {"start": v(7000, 4075) * mm, "end": v(7000, 13250) * mm});
            skLineSegment(sketch, "E217", {"start": v(-3000, 20000) * mm, "end": v(-3000, 12250) * mm});
            skLineSegment(sketch, "E218", {"start": v(-3000, 12250) * mm, "end": v(0, 12250) * mm});
            skLineSegment(sketch, "E219", {"start": v(0, 12250) * mm, "end": v(0, 14750) * mm});
            skLineSegment(sketch, "E220", {"start": v(0, 14750) * mm, "end": v(1500, 14750) * mm});
            skLineSegment(sketch, "E221", {"start": v(1500, 14750) * mm, "end": v(1500, 17250) * mm});
            skLineSegment(sketch, "E222", {"start": v(1500, 17250) * mm, "end": v(6500, 17250) * mm});
            skLineSegment(sketch, "E223", {"start": v(6500, 17250) * mm, "end": v(6500, 13250) * mm});
            skLineSegment(sketch, "E224", {"start": v(6500, 13250) * mm, "end": v(7000, 13250) * mm});
            skSolve(sketch);
        }
        {
            var Q0;
            Q0 = qSketchRegion(id + "F59", true);
            extrude(context, id + "F60", {"entities" : qUnion([Q0]), "oppositeDirection" : true, "depth" : 25 * mm, "offsetDistance" : 25 * mm});
        }
        {
            var Q0;
            Q0=qCreatedBy(makeId("Top.planeOp"),FACE);
            var sketch = newSketch(context, id + "F61", { "sketchPlane" : qUnion([Q0])});
            skLineSegment(sketch, "E225.bottom", {"start": v(11150, 16150) * mm, "end": v(14150, 16150) * mm});
            skLineSegment(sketch, "E225.top", {"start": v(11150, 9150) * mm, "end": v(14150, 9150) * mm});
            skLineSegment(sketch, "E225.left", {"start": v(11150, 16150) * mm, "end": v(11150, 9150) * mm});
            skLineSegment(sketch, "E225.right", {"start": v(14150, 16150) * mm, "end": v(14150, 9150) * mm});
            skSolve(sketch);
        }
        {
            var Q0;
            Q0 = qSketchRegion(id + "F61", true);
            extrude(context, id + "F62", {"entities" : qUnion([Q0]), "depth" : 2400 * mm, "offsetDistance" : 25 * mm});
        }
        {
            var Q0;
            Q0=qCreatedBy(makeId("Top.planeOp"),FACE);
            var sketch = newSketch(context, id + "F63", { "sketchPlane" : qUnion([Q0])});
            skCircle(sketch, "E226", {"center": v(-982.12, 17554.77) * mm, "radius": 1525 * mm});
            skSolve(sketch);
        }
        {
            var Q0;
            Q0 = qSketchRegion(id + "F63", true);
            extrude(context, id + "F64", {"entities" : qUnion([Q0]), "depth" : 200 * mm, "offsetDistance" : 25 * mm});
        }
        {
            var Q0;
            Q0=makeQuery(id+"F64.opExtrude","CAP_FACE",FACE,{"disambiguationData":[OSD([sQuery(id+"F63.wireOp",EDGE,"E226")])],"isStart":false});
            var sketch = newSketch(context, id + "F65", { "sketchPlane" : qUnion([Q0])});
            skCircle(sketch, "E227", {"center": v(-982.12, 17554.77) * mm, "radius": 1525 * mm});
            skCircle(sketch, "E228", {"center": v(-982.12, 17554.77) * mm, "radius": 1515 * mm});
            skSolve(sketch);
        }
        {
            var Q0;
            Q0 = qSketchRegion(id + "F65", true);
            extrude(context, id + "F66", {"entities" : qUnion([Q0]), "depth" : 1800 * mm, "offsetDistance" : 25 * mm});
        }
        {
            var Q0;
            Q0=qCreatedBy(makeId("Top.planeOp"),FACE);
            var sketch = newSketch(context, id + "F67", { "sketchPlane" : qUnion([Q0])});
            skLineSegment(sketch, "E229", {"start": v(7199.4, 4094.81) * mm, "end": v(7230.14, 4120.42) * mm});
            skLineSegment(sketch, "E230", {"start": v(7230.14, 4120.42) * mm, "end": v(6621.98, 4850.21) * mm});
            skLineSegment(sketch, "E231", {"start": v(6621.98, 4850.21) * mm, "end": v(6596.45, 4828.94) * mm});
            skLineSegment(sketch, "E232", {"start": v(6596.45, 4828.94) * mm, "end": v(7199.4, 4094.81) * mm});
            skLineSegment(sketch, "E233.bottom", {"start": v(7140, 4075) * mm, "end": v(7200, 4075) * mm, "construction": true});
            skLineSegment(sketch, "E233.top", {"start": v(7140, 4015) * mm, "end": v(7200, 4015) * mm, "construction": true});
            skLineSegment(sketch, "E233.left", {"start": v(7140, 4075) * mm, "end": v(7140, 4015) * mm, "construction": true});
            skLineSegment(sketch, "E233.right", {"start": v(7200, 4075) * mm, "end": v(7200, 4015) * mm, "construction": true});
            skSolve(sketch);
        }
        {
            var Q0;
            Q0 = qSketchRegion(id + "F67", true);
            extrude(context, id + "F68", {"entities" : qUnion([Q0]), "oppositeDirection" : true, "depth" : 25 * mm, "offsetDistance" : 25 * mm});
        }
        {
            var Q0;
            Q0=qCreatedBy(makeId("Top.planeOp"),FACE);
            var sketch = newSketch(context, id + "F69", { "sketchPlane" : qUnion([Q0])});
            skCircle(sketch, "E234", {"center": v(1500, -1000) * mm, "radius": 300 * mm});
            skSolve(sketch);
        }
        {
            var Q0;
            Q0 = qSketchRegion(id + "F69", true);
            extrude(context, id + "F70", {"entities" : qUnion([Q0]), "depth" : 10 * mm, "offsetDistance" : 25 * mm});
        }
        {
            var Q0;
            Q0=makeQuery(id+"F70.opExtrude","CAP_FACE",FACE,{"disambiguationData":[OSD([sQuery(id+"F69.wireOp",EDGE,"E234")])],"isStart":false});
            var sketch = newSketch(context, id + "F71", { "sketchPlane" : qUnion([Q0])});
            skLineSegment(sketch, "E235.bottom", {"start": v(6000, -750) * mm, "end": v(6250, -750) * mm});
            skLineSegment(sketch, "E235.top", {"start": v(6000, -1250) * mm, "end": v(6250, -1250) * mm});
            skLineSegment(sketch, "E235.left", {"start": v(6000, -750) * mm, "end": v(6000, -1250) * mm});
            skLineSegment(sketch, "E235.right", {"start": v(6250, -750) * mm, "end": v(6250, -1250) * mm});
            skLineSegment(sketch, "E236.1.0.0", {"start": v(5500, -1250) * mm, "end": v(5750, -1250) * mm});
            skLineSegment(sketch, "E236.1.0.1", {"start": v(5500, -750) * mm, "end": v(5750, -750) * mm});
            skLineSegment(sketch, "E236.1.0.2", {"start": v(5750, -750) * mm, "end": v(5750, -1250) * mm});
            skLineSegment(sketch, "E236.1.0.3", {"start": v(5500, -750) * mm, "end": v(5500, -1250) * mm});
            skLineSegment(sketch, "E236.2.0.0", {"start": v(5000, -1250) * mm, "end": v(5250, -1250) * mm});
            skLineSegment(sketch, "E236.2.0.1", {"start": v(5000, -750) * mm, "end": v(5250, -750) * mm});
            skLineSegment(sketch, "E236.2.0.2", {"start": v(5250, -750) * mm, "end": v(5250, -1250) * mm});
            skLineSegment(sketch, "E236.2.0.3", {"start": v(5000, -750) * mm, "end": v(5000, -1250) * mm});
            skLineSegment(sketch, "E236.3.0.0", {"start": v(4500, -1250) * mm, "end": v(4750, -1250) * mm});
            skLineSegment(sketch, "E236.3.0.1", {"start": v(4500, -750) * mm, "end": v(4750, -750) * mm});
            skLineSegment(sketch, "E236.3.0.2", {"start": v(4750, -750) * mm, "end": v(4750, -1250) * mm});
            skLineSegment(sketch, "E236.3.0.3", {"start": v(4500, -750) * mm, "end": v(4500, -1250) * mm});
            skLineSegment(sketch, "E236.4.0.0", {"start": v(4000, -1250) * mm, "end": v(4250, -1250) * mm});
            skLineSegment(sketch, "E236.4.0.1", {"start": v(4000, -750) * mm, "end": v(4250, -750) * mm});
            skLineSegment(sketch, "E236.4.0.2", {"start": v(4250, -750) * mm, "end": v(4250, -1250) * mm});
            skLineSegment(sketch, "E236.4.0.3", {"start": v(4000, -750) * mm, "end": v(4000, -1250) * mm});
            skLineSegment(sketch, "E236.5.0.0", {"start": v(3500, -1250) * mm, "end": v(3750, -1250) * mm});
            skLineSegment(sketch, "E236.5.0.1", {"start": v(3500, -750) * mm, "end": v(3750, -750) * mm});
            skLineSegment(sketch, "E236.5.0.2", {"start": v(3750, -750) * mm, "end": v(3750, -1250) * mm});
            skLineSegment(sketch, "E236.5.0.3", {"start": v(3500, -750) * mm, "end": v(3500, -1250) * mm});
            skLineSegment(sketch, "E236.6.0.0", {"start": v(3000, -1250) * mm, "end": v(3250, -1250) * mm});
            skLineSegment(sketch, "E236.6.0.1", {"start": v(3000, -750) * mm, "end": v(3250, -750) * mm});
            skLineSegment(sketch, "E236.6.0.2", {"start": v(3250, -750) * mm, "end": v(3250, -1250) * mm});
            skLineSegment(sketch, "E236.6.0.3", {"start": v(3000, -750) * mm, "end": v(3000, -1250) * mm});
            skLineSegment(sketch, "E236.7.0.0", {"start": v(2500, -1250) * mm, "end": v(2750, -1250) * mm});
            skLineSegment(sketch, "E236.7.0.1", {"start": v(2500, -750) * mm, "end": v(2750, -750) * mm});
            skLineSegment(sketch, "E236.7.0.2", {"start": v(2750, -750) * mm, "end": v(2750, -1250) * mm});
            skLineSegment(sketch, "E236.7.0.3", {"start": v(2500, -750) * mm, "end": v(2500, -1250) * mm});
            skLineSegment(sketch, "E236.8.0.0", {"start": v(2000, -1250) * mm, "end": v(2250, -1250) * mm});
            skLineSegment(sketch, "E236.8.0.1", {"start": v(2000, -750) * mm, "end": v(2250, -750) * mm});
            skLineSegment(sketch, "E236.8.0.2", {"start": v(2250, -750) * mm, "end": v(2250, -1250) * mm});
            skLineSegment(sketch, "E236.8.0.3", {"start": v(2000, -750) * mm, "end": v(2000, -1250) * mm});
            skLineSegment(sketch, "E236.direction1", {"start": v(6000, -1250) * mm, "end": v(5500, -1250) * mm, "construction": true});
            skSolve(sketch);
        }
        {
            var Q0;
            Q0 = qSketchRegion(id + "F71", true);
            extrude(context, id + "F72", {"entities" : qUnion([Q0]), "depth" : 10 * mm, "offsetDistance" : 25 * mm});
        }
        {
            var Q0;
            Q0=qCreatedBy(makeId("Top.planeOp"),FACE);
            var sketch = newSketch(context, id + "F73", { "sketchPlane" : qUnion([Q0])});
            skLineSegment(sketch, "E237", {"start": v(-3000, -5000) * mm, "end": v(-3000, -5081.78) * mm});
            skLineSegment(sketch, "E238", {"start": v(-3000, -5081.78) * mm, "end": v(11150, -2081.78) * mm});
            skLineSegment(sketch, "E239", {"start": v(11150, -2081.78) * mm, "end": v(11150, -2000) * mm});
            skLineSegment(sketch, "E240", {"start": v(11150, -2000) * mm, "end": v(-3000, -5000) * mm});
            skSolve(sketch);
        }
        {
            var Q0;
            Q0 = qSketchRegion(id + "F73", true);
            extrude(context, id + "F74", {"entities" : qUnion([Q0]), "oppositeDirection" : true, "depth" : 25 * mm, "offsetDistance" : 25 * mm});
        }
        {
            var Q0;
            Q0=qCreatedBy(makeId("Top.planeOp"),FACE);
            var sketch = newSketch(context, id + "F75", { "sketchPlane" : qUnion([Q0])});
            skLineSegment(sketch, "E241", {"start": v(-3000, -5081.78) * mm, "end": v(-3000, -7126.23) * mm});
            skLineSegment(sketch, "E242", {"start": v(-3000, -7126.23) * mm, "end": v(11150, -4126.23) * mm});
            skLineSegment(sketch, "E243", {"start": v(11150, -4126.23) * mm, "end": v(11150, -2081.78) * mm});
            skLineSegment(sketch, "E244", {"start": v(11150, -2081.78) * mm, "end": v(-3000, -5081.78) * mm});
            skSolve(sketch);
        }
        {
            var Q0;
            Q0 = qSketchRegion(id + "F75", true);
            extrude(context, id + "F76", {"entities" : qUnion([Q0]), "oppositeDirection" : true, "depth" : 25 * mm, "offsetDistance" : 25 * mm});
        }
        {
            var Q0;
            Q0=makeQuery(id+"F19.boolean.opBoolean","MERGE",FACE,{"derivedFrom":[makeQuery(id+"F14.opExtrude","SWEPT_FACE",FACE,{"disambiguationData":[OSD([sQuery(id+"F13.wireOp",EDGE,"E75.top")])]}),makeQuery(id+"F14.opExtrude","SWEPT_FACE",FACE,{"disambiguationData":[OSD([sQuery(id+"F13.wireOp",EDGE,"E92.trimOffspring")])]}),makeQuery(id+"F19.opExtrude","SWEPT_FACE",FACE,{"disambiguationData":[OSD([sQuery(id+"F18.wireOp",EDGE,"E101.top")])]})]});
            var sketch = newSketch(context, id + "F77", { "sketchPlane" : qUnion([Q0])});
            skLineSegment(sketch, "E245.bottom", {"start": v(-1710, 5340) * mm, "end": v(-2280, 5340) * mm});
            skLineSegment(sketch, "E245.top", {"start": v(-1710, 2770) * mm, "end": v(-2280, 2770) * mm});
            skLineSegment(sketch, "E245.left", {"start": v(-1710, 5340) * mm, "end": v(-1710, 2770) * mm});
            skLineSegment(sketch, "E245.right", {"start": v(-2280, 5340) * mm, "end": v(-2280, 2770) * mm});
            skLineSegment(sketch, "E246.bottom", {"start": v(-3745, 4820) * mm, "end": v(-5945, 4820) * mm});
            skLineSegment(sketch, "E246.top", {"start": v(-3745, 3970) * mm, "end": v(-5945, 3970) * mm});
            skLineSegment(sketch, "E246.left", {"start": v(-3745, 4820) * mm, "end": v(-3745, 3970) * mm});
            skLineSegment(sketch, "E246.right", {"start": v(-5945, 4820) * mm, "end": v(-5945, 3970) * mm});
            skLineSegment(sketch, "E247.bottom", {"start": v(-1310, 7780) * mm, "end": v(-3360, 7780) * mm});
            skLineSegment(sketch, "E247.top", {"start": v(-1310, 6930) * mm, "end": v(-3360, 6930) * mm});
            skLineSegment(sketch, "E247.left", {"start": v(-1310, 7780) * mm, "end": v(-1310, 6930) * mm});
            skLineSegment(sketch, "E247.right", {"start": v(-3360, 7780) * mm, "end": v(-3360, 6930) * mm});
            skLineSegment(sketch, "E248.bottom", {"start": v(-2280, 2270) * mm, "end": v(-1710, 2270) * mm});
            skLineSegment(sketch, "E248.top", {"start": v(-2280, 0) * mm, "end": v(-1710, 0) * mm});
            skLineSegment(sketch, "E248.left", {"start": v(-2280, 2270) * mm, "end": v(-2280, 0) * mm});
            skLineSegment(sketch, "E248.right", {"start": v(-1710, 2270) * mm, "end": v(-1710, 0) * mm});
            skLineSegment(sketch, "E249.bottom", {"start": v(-3745, 2050) * mm, "end": v(-5945, 2050) * mm});
            skLineSegment(sketch, "E249.top", {"start": v(-3745, 1200) * mm, "end": v(-5945, 1200) * mm});
            skLineSegment(sketch, "E249.left", {"start": v(-3745, 2050) * mm, "end": v(-3745, 1200) * mm});
            skLineSegment(sketch, "E249.right", {"start": v(-5945, 2050) * mm, "end": v(-5945, 1200) * mm});
            skLineSegment(sketch, "E250.0", {"start": v(-1360, 7730) * mm, "end": v(-3310, 7730) * mm});
            skLineSegment(sketch, "E250.1", {"start": v(-1360, 7730) * mm, "end": v(-1360, 6980) * mm});
            skLineSegment(sketch, "E250.2", {"start": v(-1360, 6980) * mm, "end": v(-3310, 6980) * mm});
            skLineSegment(sketch, "E250.3", {"start": v(-3310, 7730) * mm, "end": v(-3310, 6980) * mm});
            skLineSegment(sketch, "E251.0", {"start": v(-3795, 4020) * mm, "end": v(-5895, 4020) * mm});
            skLineSegment(sketch, "E251.1", {"start": v(-3795, 4770) * mm, "end": v(-3795, 4020) * mm});
            skLineSegment(sketch, "E251.2", {"start": v(-3795, 4770) * mm, "end": v(-5895, 4770) * mm});
            skLineSegment(sketch, "E251.3", {"start": v(-5895, 4770) * mm, "end": v(-5895, 4020) * mm});
            skLineSegment(sketch, "E252.0", {"start": v(-1760, 2820) * mm, "end": v(-2230, 2820) * mm});
            skLineSegment(sketch, "E252.1", {"start": v(-1760, 5290) * mm, "end": v(-1760, 2820) * mm});
            skLineSegment(sketch, "E252.2", {"start": v(-1760, 5290) * mm, "end": v(-2230, 5290) * mm});
            skLineSegment(sketch, "E252.3", {"start": v(-2230, 5290) * mm, "end": v(-2230, 2820) * mm});
            skLineSegment(sketch, "E253.0", {"start": v(-3795, 1250) * mm, "end": v(-5895, 1250) * mm});
            skLineSegment(sketch, "E253.1", {"start": v(-3795, 2000) * mm, "end": v(-3795, 1250) * mm});
            skLineSegment(sketch, "E253.2", {"start": v(-3795, 2000) * mm, "end": v(-5895, 2000) * mm});
            skLineSegment(sketch, "E253.3", {"start": v(-5895, 2000) * mm, "end": v(-5895, 1250) * mm});
            skLineSegment(sketch, "E254.0", {"start": v(-2230, 50) * mm, "end": v(-1760, 50) * mm});
            skLineSegment(sketch, "E254.1", {"start": v(-2230, 2220) * mm, "end": v(-2230, 50) * mm});
            skLineSegment(sketch, "E254.2", {"start": v(-2230, 2220) * mm, "end": v(-1760, 2220) * mm});
            skLineSegment(sketch, "E254.3", {"start": v(-1760, 2220) * mm, "end": v(-1760, 50) * mm});
            skSolve(sketch);
        }
        {
            var Q0;
            Q0 = qSketchRegion(id + "F77", true);
            extrude(context, id + "F78", {"entities" : qUnion([Q0]), "oppositeDirection" : true, "depth" : 250 * mm, "offsetDistance" : 25 * mm});
        }
        {
            var Q0;
            Q0=makeQuery(id+"F19.boolean.opBoolean","MERGE",FACE,{"derivedFrom":[makeQuery(id+"F14.opExtrude","SWEPT_FACE",FACE,{"disambiguationData":[OSD([sQuery(id+"F13.wireOp",EDGE,"E75.right")])]}),makeQuery(id+"F14.opExtrude","SWEPT_FACE",FACE,{"disambiguationData":[OSD([sQuery(id+"F13.wireOp",EDGE,"E84.trimOffspring")])]}),makeQuery(id+"F19.opExtrude","SWEPT_FACE",FACE,{"disambiguationData":[OSD([sQuery(id+"F18.wireOp",EDGE,"E101.right")])]})]});
            var sketch = newSketch(context, id + "F79", { "sketchPlane" : qUnion([Q0])});
            skLineSegment(sketch, "E255.0", {"start": v(-6515, 5290) * mm, "end": v(-6515, 2820) * mm});
            skLineSegment(sketch, "E255.1", {"start": v(-6515, 5290) * mm, "end": v(-8015, 5290) * mm});
            skLineSegment(sketch, "E255.2", {"start": v(-8015, 5290) * mm, "end": v(-8015, 2820) * mm});
            skLineSegment(sketch, "E255.3", {"start": v(-6515, 2820) * mm, "end": v(-8015, 2820) * mm});
            skLineSegment(sketch, "E256.0", {"start": v(-1605, 4020) * mm, "end": v(-605, 4020) * mm});
            skLineSegment(sketch, "E256.1", {"start": v(-1605, 4770) * mm, "end": v(-1605, 4020) * mm});
            skLineSegment(sketch, "E256.2", {"start": v(-1605, 4770) * mm, "end": v(-605, 4770) * mm});
            skLineSegment(sketch, "E256.3", {"start": v(-605, 4770) * mm, "end": v(-605, 4020) * mm});
            skLineSegment(sketch, "E257.0", {"start": v(-1605, 1250) * mm, "end": v(-605, 1250) * mm});
            skLineSegment(sketch, "E257.1", {"start": v(-1605, 2000) * mm, "end": v(-1605, 1250) * mm});
            skLineSegment(sketch, "E257.2", {"start": v(-1605, 2000) * mm, "end": v(-605, 2000) * mm});
            skLineSegment(sketch, "E257.3", {"start": v(-605, 2000) * mm, "end": v(-605, 1250) * mm});
            skLineSegment(sketch, "E258.bottom", {"start": v(-5665, 2270) * mm, "end": v(-8065, 2270) * mm});
            skLineSegment(sketch, "E258.top", {"start": v(-5665, 0) * mm, "end": v(-8065, 0) * mm});
            skLineSegment(sketch, "E258.left", {"start": v(-5665, 2270) * mm, "end": v(-5665, 0) * mm});
            skLineSegment(sketch, "E258.right", {"start": v(-8065, 2270) * mm, "end": v(-8065, 0) * mm});
            skLineSegment(sketch, "E259.0", {"start": v(-5715, 50) * mm, "end": v(-8015, 50) * mm});
            skLineSegment(sketch, "E259.1", {"start": v(-5715, 2220) * mm, "end": v(-5715, 50) * mm});
            skLineSegment(sketch, "E259.2", {"start": v(-5715, 2220) * mm, "end": v(-8015, 2220) * mm});
            skLineSegment(sketch, "E259.3", {"start": v(-8015, 2220) * mm, "end": v(-8015, 50) * mm});
            skLineSegment(sketch, "E260.bottom", {"start": v(-555, 2050) * mm, "end": v(-1655, 2050) * mm});
            skLineSegment(sketch, "E260.top", {"start": v(-555, 1200) * mm, "end": v(-1655, 1200) * mm});
            skLineSegment(sketch, "E260.left", {"start": v(-555, 2050) * mm, "end": v(-555, 1200) * mm});
            skLineSegment(sketch, "E260.right", {"start": v(-1655, 2050) * mm, "end": v(-1655, 1200) * mm});
            skLineSegment(sketch, "E261.bottom", {"start": v(-1655, 3970) * mm, "end": v(-555, 3970) * mm});
            skLineSegment(sketch, "E261.top", {"start": v(-1655, 4820) * mm, "end": v(-555, 4820) * mm});
            skLineSegment(sketch, "E261.left", {"start": v(-1655, 3970) * mm, "end": v(-1655, 4820) * mm});
            skLineSegment(sketch, "E261.right", {"start": v(-555, 3970) * mm, "end": v(-555, 4820) * mm});
            skLineSegment(sketch, "E262.bottom", {"start": v(-8065, 2770) * mm, "end": v(-6465, 2770) * mm});
            skLineSegment(sketch, "E262.top", {"start": v(-8065, 5340) * mm, "end": v(-6465, 5340) * mm});
            skLineSegment(sketch, "E262.left", {"start": v(-8065, 2770) * mm, "end": v(-8065, 5340) * mm});
            skLineSegment(sketch, "E262.right", {"start": v(-6465, 2770) * mm, "end": v(-6465, 5340) * mm});
            skSolve(sketch);
        }
        {
            var Q0;
            Q0 = qSketchRegion(id + "F79", true);
            extrude(context, id + "F80", {"entities" : qUnion([Q0]), "oppositeDirection" : true, "depth" : 250 * mm, "offsetDistance" : 25 * mm});
        }
        {
            var Q0;
            Q0=makeQuery(id+"F31.boolean.opBoolean","MERGE",FACE,{"derivedFrom":[makeQuery(id+"F26.opExtrude","SWEPT_FACE",FACE,{"disambiguationData":[OSD([sQuery(id+"F25.wireOp",EDGE,"E105.right")])]}),makeQuery(id+"F26.opExtrude","SWEPT_FACE",FACE,{"disambiguationData":[OSD([sQuery(id+"F25.wireOp",EDGE,"E112.trimOffspring")])]}),makeQuery(id+"F26.opExtrude","SWEPT_FACE",FACE,{"disambiguationData":[OSD([sQuery(id+"F25.wireOp",EDGE,"E116.trimOffspring")])]}),makeQuery(id+"F31.opExtrude","SWEPT_FACE",FACE,{"disambiguationData":[OSD([sQuery(id+"F30.wireOp",EDGE,"E127.left")])]})]});
            var sketch = newSketch(context, id + "F81", { "sketchPlane" : qUnion([Q0])});
            skLineSegment(sketch, "E263.bottom", {"start": v(-3235, 8000) * mm, "end": v(-4835, 8000) * mm});
            skLineSegment(sketch, "E263.top", {"start": v(-3235, 5840) * mm, "end": v(-4835, 5840) * mm});
            skLineSegment(sketch, "E263.left", {"start": v(-3235, 8000) * mm, "end": v(-3235, 5840) * mm});
            skLineSegment(sketch, "E263.right", {"start": v(-4835, 8000) * mm, "end": v(-4835, 5840) * mm});
            skLineSegment(sketch, "E264.0", {"start": v(-3285, 5890) * mm, "end": v(-4785, 5890) * mm});
            skLineSegment(sketch, "E264.1", {"start": v(-3285, 7950) * mm, "end": v(-3285, 5890) * mm});
            skLineSegment(sketch, "E264.2", {"start": v(-3285, 7950) * mm, "end": v(-4785, 7950) * mm});
            skLineSegment(sketch, "E264.3", {"start": v(-4785, 7950) * mm, "end": v(-4785, 5890) * mm});
            skLineSegment(sketch, "E265.bottom", {"start": v(-6465, 8000) * mm, "end": v(-8065, 8000) * mm});
            skLineSegment(sketch, "E265.top", {"start": v(-6465, 5840) * mm, "end": v(-8065, 5840) * mm});
            skLineSegment(sketch, "E265.left", {"start": v(-6465, 8000) * mm, "end": v(-6465, 5840) * mm});
            skLineSegment(sketch, "E265.right", {"start": v(-8065, 8000) * mm, "end": v(-8065, 5840) * mm});
            skLineSegment(sketch, "E266.0", {"start": v(-6515, 5890) * mm, "end": v(-8015, 5890) * mm});
            skLineSegment(sketch, "E266.1", {"start": v(-6515, 7950) * mm, "end": v(-6515, 5890) * mm});
            skLineSegment(sketch, "E266.2", {"start": v(-6515, 7950) * mm, "end": v(-8015, 7950) * mm});
            skLineSegment(sketch, "E266.3", {"start": v(-8015, 7950) * mm, "end": v(-8015, 5890) * mm});
            skSolve(sketch);
        }
        {
            var Q0;
            Q0 = qSketchRegion(id + "F81", true);
            extrude(context, id + "F82", {"entities" : qUnion([Q0]), "oppositeDirection" : true, "depth" : 250 * mm, "offsetDistance" : 25 * mm});
        }
        {
            var Q0;
            Q0=makeQuery(id+"F19.boolean.opBoolean","MERGE",FACE,{"derivedFrom":[makeQuery(id+"F14.opExtrude","SWEPT_FACE",FACE,{"disambiguationData":[OSD([sQuery(id+"F13.wireOp",EDGE,"E75.bottom"),sQuery(id+"F13.wireOp",EDGE,"E78"),sQuery(id+"F13.wireOp",EDGE,"E79")])]}),makeQuery(id+"F19.opExtrude","SWEPT_FACE",FACE,{"disambiguationData":[OSD([sQuery(id+"F18.wireOp",EDGE,"E101.bottom")])]})]});
            var sketch = newSketch(context, id + "F83", { "sketchPlane" : qUnion([Q0])});
            skLineSegment(sketch, "E267.bottom", {"start": v(4450, 3540) * mm, "end": v(2050, 3540) * mm});
            skLineSegment(sketch, "E267.top", {"start": v(4450, 4820) * mm, "end": v(2050, 4820) * mm});
            skLineSegment(sketch, "E267.left", {"start": v(4450, 3540) * mm, "end": v(4450, 4820) * mm});
            skLineSegment(sketch, "E267.right", {"start": v(2050, 3540) * mm, "end": v(2050, 4820) * mm});
            skLineSegment(sketch, "E268.bottom", {"start": v(4450, 2270) * mm, "end": v(2050, 2270) * mm});
            skLineSegment(sketch, "E268.top", {"start": v(4450, 0) * mm, "end": v(2050, 0) * mm});
            skLineSegment(sketch, "E268.left", {"start": v(4450, 2270) * mm, "end": v(4450, 0) * mm});
            skLineSegment(sketch, "E268.right", {"start": v(2050, 2270) * mm, "end": v(2050, 0) * mm});
            skLineSegment(sketch, "E269.0", {"start": v(4400, 3590) * mm, "end": v(2100, 3590) * mm});
            skLineSegment(sketch, "E269.1", {"start": v(4400, 3590) * mm, "end": v(4400, 4770) * mm});
            skLineSegment(sketch, "E269.2", {"start": v(4400, 4770) * mm, "end": v(2100, 4770) * mm});
            skLineSegment(sketch, "E269.3", {"start": v(2100, 3590) * mm, "end": v(2100, 4770) * mm});
            skLineSegment(sketch, "E270.0", {"start": v(4400, 50) * mm, "end": v(2100, 50) * mm});
            skLineSegment(sketch, "E270.1", {"start": v(4400, 2220) * mm, "end": v(4400, 50) * mm});
            skLineSegment(sketch, "E270.2", {"start": v(4400, 2220) * mm, "end": v(2100, 2220) * mm});
            skLineSegment(sketch, "E270.3", {"start": v(2100, 2220) * mm, "end": v(2100, 50) * mm});
            skSolve(sketch);
        }
        {
            var Q0;
            Q0 = qSketchRegion(id + "F83", true);
            extrude(context, id + "F84", {"entities" : qUnion([Q0]), "oppositeDirection" : true, "depth" : 250 * mm, "offsetDistance" : 25 * mm});
        }
        {
            var Q0;
            Q0=makeQuery(id+"F31.boolean.opBoolean","MERGE",FACE,{"derivedFrom":[makeQuery(id+"F26.opExtrude","SWEPT_FACE",FACE,{"disambiguationData":[OSD([sQuery(id+"F25.wireOp",EDGE,"E105.bottom")])]}),makeQuery(id+"F26.opExtrude","SWEPT_FACE",FACE,{"disambiguationData":[OSD([sQuery(id+"F25.wireOp",EDGE,"E109.trimOffspring")])]}),makeQuery(id+"F31.opExtrude","SWEPT_FACE",FACE,{"disambiguationData":[OSD([sQuery(id+"F30.wireOp",EDGE,"E127.top")])]})]});
            var sketch = newSketch(context, id + "F85", { "sketchPlane" : qUnion([Q0])});
            skLineSegment(sketch, "E271.bottom", {"start": v(4445, 8000) * mm, "end": v(2045, 8000) * mm});
            skLineSegment(sketch, "E271.top", {"start": v(4445, 5840) * mm, "end": v(2045, 5840) * mm});
            skLineSegment(sketch, "E271.left", {"start": v(4445, 8000) * mm, "end": v(4445, 5840) * mm});
            skLineSegment(sketch, "E271.right", {"start": v(2045, 8000) * mm, "end": v(2045, 5840) * mm});
            skLineSegment(sketch, "E272.0", {"start": v(4395, 5890) * mm, "end": v(2095, 5890) * mm});
            skLineSegment(sketch, "E272.1", {"start": v(4395, 7950) * mm, "end": v(4395, 5890) * mm});
            skLineSegment(sketch, "E272.2", {"start": v(4395, 7950) * mm, "end": v(2095, 7950) * mm});
            skLineSegment(sketch, "E272.3", {"start": v(2095, 7950) * mm, "end": v(2095, 5890) * mm});
            skSolve(sketch);
        }
        {
            var Q0;
            Q0 = qSketchRegion(id + "F85", true);
            extrude(context, id + "F86", {"entities" : qUnion([Q0]), "oppositeDirection" : true, "depth" : 250 * mm, "offsetDistance" : 25 * mm});
        }
        {
            var Q0;
            Q0=makeQuery(id+"F19.boolean.opBoolean","MERGE",FACE,{"derivedFrom":[makeQuery(id+"F14.opExtrude","SWEPT_FACE",FACE,{"disambiguationData":[OSD([sQuery(id+"F13.wireOp",EDGE,"E75.left")])]}),makeQuery(id+"F14.opExtrude","SWEPT_FACE",FACE,{"disambiguationData":[OSD([sQuery(id+"F13.wireOp",EDGE,"E97.trimOffspring")])]}),makeQuery(id+"F19.opExtrude","SWEPT_FACE",FACE,{"disambiguationData":[OSD([sQuery(id+"F18.wireOp",EDGE,"E101.left")])]})]});
            var sketch = newSketch(context, id + "F87", { "sketchPlane" : qUnion([Q0])});
            skLineSegment(sketch, "E273.bottom", {"start": v(4210, 5340) * mm, "end": v(3640, 5340) * mm});
            skLineSegment(sketch, "E273.top", {"start": v(4210, 2770) * mm, "end": v(3640, 2770) * mm});
            skLineSegment(sketch, "E273.left", {"start": v(4210, 5340) * mm, "end": v(4210, 2770) * mm});
            skLineSegment(sketch, "E273.right", {"start": v(3640, 5340) * mm, "end": v(3640, 2770) * mm});
            skLineSegment(sketch, "E274.bottom", {"start": v(4000, 2270) * mm, "end": v(2900, 2270) * mm});
            skLineSegment(sketch, "E274.top", {"start": v(4000, 0) * mm, "end": v(2900, 0) * mm});
            skLineSegment(sketch, "E274.left", {"start": v(4000, 2270) * mm, "end": v(4000, 0) * mm});
            skLineSegment(sketch, "E274.right", {"start": v(2900, 2270) * mm, "end": v(2900, 0) * mm});
            skLineSegment(sketch, "E275.bottom", {"start": v(1900, 2050) * mm, "end": v(1400, 2050) * mm});
            skLineSegment(sketch, "E275.top", {"start": v(1900, 1200) * mm, "end": v(1400, 1200) * mm});
            skLineSegment(sketch, "E275.left", {"start": v(1900, 2050) * mm, "end": v(1900, 1200) * mm});
            skLineSegment(sketch, "E275.right", {"start": v(1400, 2050) * mm, "end": v(1400, 1200) * mm});
            skLineSegment(sketch, "E276.0", {"start": v(1850, 1250) * mm, "end": v(1450, 1250) * mm});
            skLineSegment(sketch, "E276.1", {"start": v(1850, 2000) * mm, "end": v(1850, 1250) * mm});
            skLineSegment(sketch, "E276.2", {"start": v(1850, 2000) * mm, "end": v(1450, 2000) * mm});
            skLineSegment(sketch, "E276.3", {"start": v(1450, 2000) * mm, "end": v(1450, 1250) * mm});
            skLineSegment(sketch, "E277.0", {"start": v(3950, 50) * mm, "end": v(2950, 50) * mm});
            skLineSegment(sketch, "E277.1", {"start": v(3950, 2220) * mm, "end": v(3950, 50) * mm});
            skLineSegment(sketch, "E277.2", {"start": v(3950, 2220) * mm, "end": v(2950, 2220) * mm});
            skLineSegment(sketch, "E277.3", {"start": v(2950, 2220) * mm, "end": v(2950, 50) * mm});
            skLineSegment(sketch, "E278.0", {"start": v(4160, 2820) * mm, "end": v(3690, 2820) * mm});
            skLineSegment(sketch, "E278.1", {"start": v(4160, 5290) * mm, "end": v(4160, 2820) * mm});
            skLineSegment(sketch, "E278.2", {"start": v(4160, 5290) * mm, "end": v(3690, 5290) * mm});
            skLineSegment(sketch, "E278.3", {"start": v(3690, 5290) * mm, "end": v(3690, 2820) * mm});
            skSolve(sketch);
        }
        {
            var Q0;
            Q0 = qSketchRegion(id + "F87", true);
            extrude(context, id + "F88", {"entities" : qUnion([Q0]), "oppositeDirection" : true, "depth" : 250 * mm, "offsetDistance" : 25 * mm});
        }
        {
            var Q0;
            Q0=makeQuery(id+"F42.boolean.opBoolean","MERGE",FACE,{"derivedFrom":[makeQuery(id+"F40.boolean.opBoolean","MERGE",FACE,{"derivedFrom":[makeQuery(id+"F38.opExtrude","SWEPT_FACE",FACE,{"disambiguationData":[OSD([sQuery(id+"F37.wireOp",EDGE,"E145.bottom")])]}),makeQuery(id+"F38.opExtrude","SWEPT_FACE",FACE,{"disambiguationData":[OSD([sQuery(id+"F37.wireOp",EDGE,"E154.trimOffspring")])]}),makeQuery(id+"F40.opExtrude","SWEPT_FACE",FACE,{"disambiguationData":[OSD([sQuery(id+"F39.wireOp",EDGE,"E155.top")])]})]}),makeQuery(id+"F42.opExtrude","SWEPT_FACE",FACE,{"disambiguationData":[OSD([sQuery(id+"F41.wireOp",EDGE,"E156.top")])]})]});
            var sketch = newSketch(context, id + "F89", { "sketchPlane" : qUnion([Q0])});
            skLineSegment(sketch, "E279.bottom", {"start": v(-2850, 2200) * mm, "end": v(-150, 2200) * mm});
            skLineSegment(sketch, "E279.top", {"start": v(-2850, 0) * mm, "end": v(-150, 0) * mm});
            skLineSegment(sketch, "E279.left", {"start": v(-2850, 2200) * mm, "end": v(-2850, 0) * mm});
            skLineSegment(sketch, "E279.right", {"start": v(-150, 2200) * mm, "end": v(-150, 0) * mm});
            skSolve(sketch);
        }
        {
            var Q0;
            Q0 = qSketchRegion(id + "F89", true);
            extrude(context, id + "F90", {"entities" : qUnion([Q0]), "operationType" : NewBodyOperationType.ADD, "oppositeDirection" : true, "depth" : 25 * mm, "offsetDistance" : 25 * mm});
        }
        {
            var Q0;
            Q0=makeQuery(id+"F42.boolean.opBoolean","MERGE",FACE,{"derivedFrom":[makeQuery(id+"F40.boolean.opBoolean","MERGE",FACE,{"derivedFrom":[makeQuery(id+"F38.opExtrude","SWEPT_FACE",FACE,{"disambiguationData":[OSD([sQuery(id+"F37.wireOp",EDGE,"E145.top")])]}),makeQuery(id+"F38.opExtrude","SWEPT_FACE",FACE,{"disambiguationData":[OSD([sQuery(id+"F37.wireOp",EDGE,"E149.trimOffspring")])]}),makeQuery(id+"F40.opExtrude","SWEPT_FACE",FACE,{"disambiguationData":[OSD([sQuery(id+"F39.wireOp",EDGE,"E155.bottom")])]})]}),makeQuery(id+"F42.opExtrude","SWEPT_FACE",FACE,{"disambiguationData":[OSD([sQuery(id+"F41.wireOp",EDGE,"E156.bottom")])]})]});
            var sketch = newSketch(context, id + "F91", { "sketchPlane" : qUnion([Q0])});
            skLineSegment(sketch, "E280.bottom", {"start": v(1750, 2200) * mm, "end": v(2600, 2200) * mm});
            skLineSegment(sketch, "E280.top", {"start": v(1750, 0) * mm, "end": v(2600, 0) * mm});
            skLineSegment(sketch, "E280.left", {"start": v(1750, 2200) * mm, "end": v(1750, 0) * mm});
            skLineSegment(sketch, "E280.right", {"start": v(2600, 2200) * mm, "end": v(2600, 0) * mm});
            skSolve(sketch);
        }
        {
            var Q0;
            Q0 = qSketchRegion(id + "F91", true);
            extrude(context, id + "F92", {"entities" : qUnion([Q0]), "oppositeDirection" : true, "depth" : 25 * mm, "offsetDistance" : 25 * mm});
        }
    });
